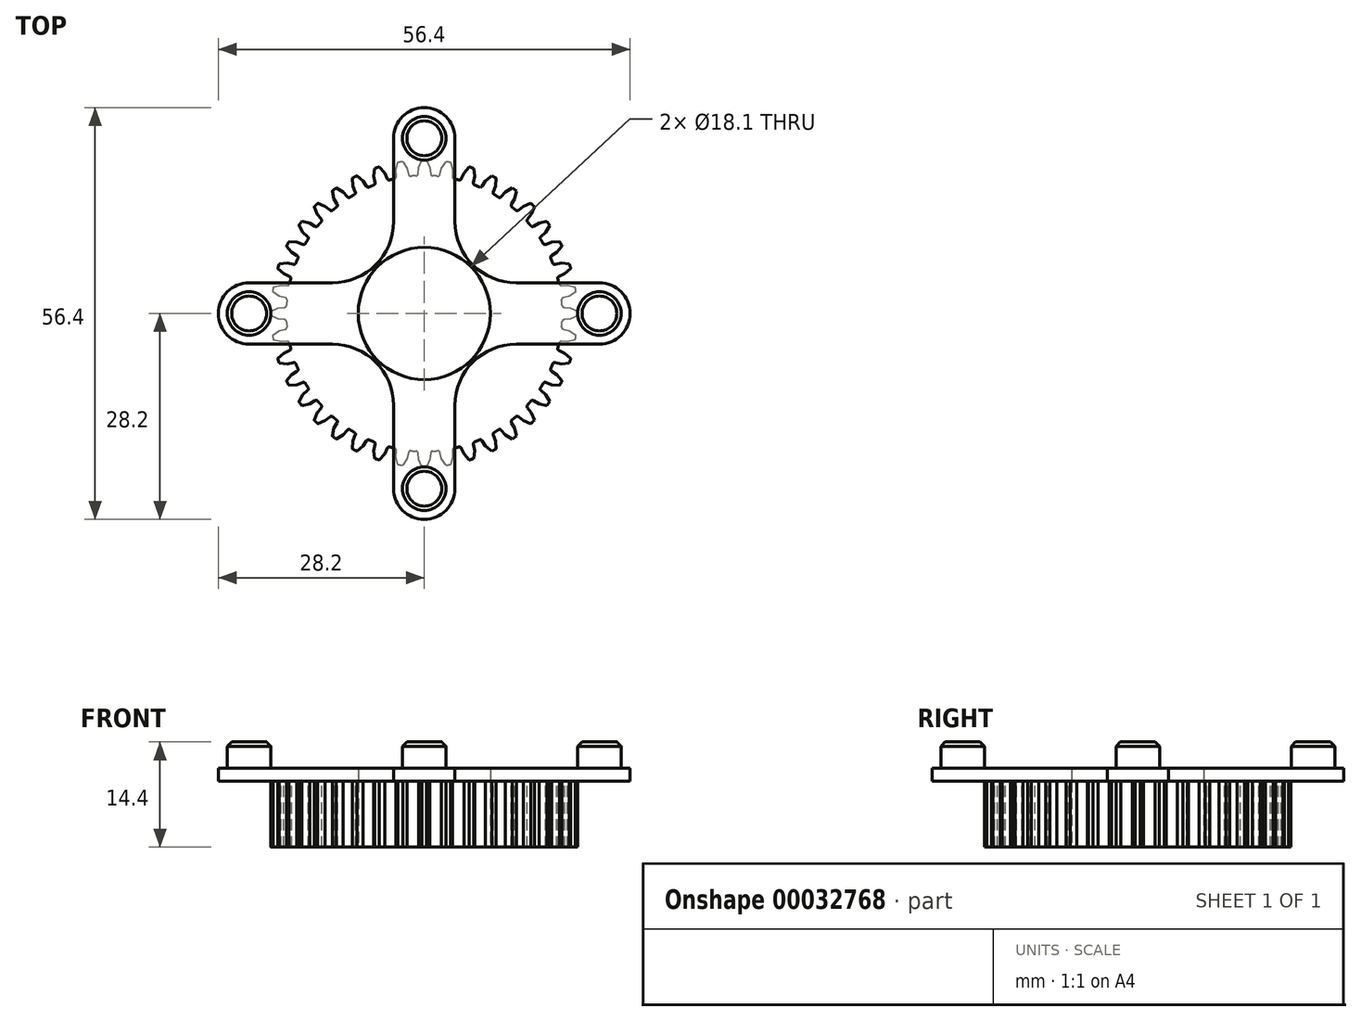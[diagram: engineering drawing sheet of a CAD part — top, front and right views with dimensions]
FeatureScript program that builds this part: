
annotation { "Feature Type Name" : "Feature", "Feature Type Description" : "" }
export const myFeature = defineFeature(function(context is Context, id is Id, definition is map)
    precondition{}
    {
        {
            var Q0;
            Q0=qCreatedBy(makeId("Top.planeOp"),FACE);
            var sketch = newSketch(context, id + "F0", { "sketchPlane" : qUnion([Q0])});
            skCircle(sketch, "E0", {"center": v(0, 0) * mm, "radius": 1 * mm});
            skCircle(sketch, "E1", {"center": v(0, 0) * mm, "radius": 52.75 * mm});
            skCircle(sketch, "E2", {"center": v(0, 40) * mm, "radius": 1 * mm});
            skCircle(sketch, "E3", {"center": v(40, 0) * mm, "radius": 1 * mm});
            skCircle(sketch, "E4", {"center": v(0, -40) * mm, "radius": 1 * mm});
            skCircle(sketch, "E5", {"center": v(-40, 0) * mm, "radius": 1 * mm});
            skCircle(sketch, "E6", {"center": v(0, 40) * mm, "radius": 4.97 * mm});
            skCircle(sketch, "E7", {"center": v(-40, 0) * mm, "radius": 4.97 * mm});
            skCircle(sketch, "E8", {"center": v(40, 0) * mm, "radius": 4.97 * mm});
            skCircle(sketch, "E9", {"center": v(0, -40) * mm, "radius": 4.97 * mm});
            skCircle(sketch, "E10", {"center": v(0, 0) * mm, "radius": 40 * mm, "construction": true});
            skArc(sketch, "E11.0.startCap", {"start": v(-7, 40) * mm, "mid": v(0, 47) * mm, "end": v(7, 40) * mm});
            skArc(sketch, "E11.0.endCap", {"start": v(7, -40) * mm, "mid": v(0, -47) * mm, "end": v(-7, -40) * mm});
            skLineSegment(sketch, "E11.0.left", {"start": v(7, 40) * mm, "end": v(7, 21) * mm});
            skLineSegment(sketch, "E11.0.right", {"start": v(-7, 40) * mm, "end": v(-7, 21) * mm});
            skArc(sketch, "E12.0.startCap", {"start": v(40, 7) * mm, "mid": v(47, 0) * mm, "end": v(40, -7) * mm});
            skArc(sketch, "E12.0.endCap", {"start": v(-40, -7) * mm, "mid": v(-47, 0) * mm, "end": v(-40, 7) * mm});
            skLineSegment(sketch, "E12.0.left", {"start": v(40, -7) * mm, "end": v(21, -7) * mm});
            skLineSegment(sketch, "E12.0.right", {"start": v(40, 7) * mm, "end": v(21, 7) * mm});
            skLineSegment(sketch, "E13.trimOffspring", {"start": v(-21, 7) * mm, "end": v(-40, 7) * mm});
            skLineSegment(sketch, "E14.trimOffspring", {"start": v(-7, -21) * mm, "end": v(-7, -40) * mm});
            skLineSegment(sketch, "E15.trimOffspring", {"start": v(7, -21) * mm, "end": v(7, -40) * mm});
            skLineSegment(sketch, "E16.trimOffspring", {"start": v(-21, -7) * mm, "end": v(-40, -7) * mm});
            skPoint(sketch, "E17.visualSharp", {"position": v(-7, 7) * mm});
            skArc(sketch, "E17.filletArc", {"start": v(-21, 7) * mm, "mid": v(-11.1, 11.1) * mm, "end": v(-7, 21) * mm});
            skPoint(sketch, "E18.visualSharp", {"position": v(-7, -7) * mm});
            skArc(sketch, "E18.filletArc", {"start": v(-7, -21) * mm, "mid": v(-11.1, -11.1) * mm, "end": v(-21, -7) * mm});
            skPoint(sketch, "E19.visualSharp", {"position": v(7, -7) * mm});
            skArc(sketch, "E19.filletArc", {"start": v(21, -7) * mm, "mid": v(11.1, -11.1) * mm, "end": v(7, -21) * mm});
            skPoint(sketch, "E20.visualSharp", {"position": v(7, 7) * mm});
            skArc(sketch, "E20.filletArc", {"start": v(7, 21) * mm, "mid": v(11.1, 11.1) * mm, "end": v(21, 7) * mm});
            skCircle(sketch, "E21", {"center": v(0, 0) * mm, "radius": 5 * mm});
            skCircle(sketch, "E22", {"center": v(0, 0) * mm, "radius": 14 * mm});
            skCircle(sketch, "E23", {"center": v(0, 0) * mm, "radius": 47 * mm, "construction": true});
            skSolve(sketch);
        }
        {
            var Q0;
            Q0=makeQuery(id+"F0.imprint","IMPRINT",FACE,{"disambiguationData":[TD([[makeQuery(id+"F0.imprint","IMPRINT",EDGE,{"derivedFrom":sQuery(id+"F0.wireOp",EDGE,"E6")}),-1.0]])]});
            var Q1;
            Q1=makeQuery(id+"F0.imprint","IMPRINT",FACE,{"disambiguationData":[TD([[makeQuery(id+"F0.imprint","IMPRINT",EDGE,{"derivedFrom":sQuery(id+"F0.wireOp",EDGE,"E5")}),1.0]])]});
            var Q2;
            Q2=makeQuery(id+"F0.imprint","IMPRINT",FACE,{"disambiguationData":[TD([[makeQuery(id+"F0.imprint","IMPRINT",EDGE,{"derivedFrom":sQuery(id+"F0.wireOp",EDGE,"E21")}),-1.0]])]});
            var Q3;
            Q3=makeQuery(id+"F0.imprint","IMPRINT",FACE,{"disambiguationData":[TD([[makeQuery(id+"F0.imprint","IMPRINT",EDGE,{"derivedFrom":sQuery(id+"F0.wireOp",EDGE,"E3")}),1.0]])]});
            var Q4;
            Q4=makeQuery(id+"F0.imprint","IMPRINT",FACE,{"disambiguationData":[TD([[makeQuery(id+"F0.imprint","IMPRINT",EDGE,{"derivedFrom":sQuery(id+"F0.wireOp",EDGE,"E2")}),1.0]])]});
            var Q5;
            Q5=makeQuery(id+"F0.imprint","IMPRINT",FACE,{"disambiguationData":[TD([[makeQuery(id+"F0.imprint","IMPRINT",EDGE,{"derivedFrom":sQuery(id+"F0.wireOp",EDGE,"E4")}),1.0]])]});
            var Q6;
            Q6=makeQuery(id+"F0.imprint","IMPRINT",FACE,{"disambiguationData":[TD([[makeQuery(id+"F0.imprint","IMPRINT",EDGE,{"derivedFrom":sQuery(id+"F0.wireOp",EDGE,"E5")}),-1.0]])]});
            var Q7;
            Q7=makeQuery(id+"F0.imprint","IMPRINT",FACE,{"disambiguationData":[TD([[makeQuery(id+"F0.imprint","IMPRINT",EDGE,{"derivedFrom":sQuery(id+"F0.wireOp",EDGE,"E4")}),-1.0]])]});
            var Q8;
            Q8=makeQuery(id+"F0.imprint","IMPRINT",FACE,{"disambiguationData":[TD([[makeQuery(id+"F0.imprint","IMPRINT",EDGE,{"derivedFrom":sQuery(id+"F0.wireOp",EDGE,"E3")}),-1.0]])]});
            var Q9;
            Q9=makeQuery(id+"F0.imprint","IMPRINT",FACE,{"disambiguationData":[TD([[makeQuery(id+"F0.imprint","IMPRINT",EDGE,{"derivedFrom":sQuery(id+"F0.wireOp",EDGE,"E2")}),-1.0]])]});
            extrude(context, id + "F1", {"entities" : qUnion([Q0, Q1, Q2, Q3, Q4, Q5, Q6, Q7, Q8, Q9]), "depth" : 3 * mm});
        }
        {
            var Q0;
            Q0=makeQuery(id+"F0.imprint","IMPRINT",FACE,{"disambiguationData":[TD([[makeQuery(id+"F0.imprint","IMPRINT",EDGE,{"derivedFrom":sQuery(id+"F0.wireOp",EDGE,"E5")}),1.0]])]});
            var Q1;
            Q1=makeQuery(id+"F0.imprint","IMPRINT",FACE,{"disambiguationData":[TD([[makeQuery(id+"F0.imprint","IMPRINT",EDGE,{"derivedFrom":sQuery(id+"F0.wireOp",EDGE,"E5")}),-1.0]])]});
            var Q2;
            Q2=makeQuery(id+"F0.imprint","IMPRINT",FACE,{"disambiguationData":[TD([[makeQuery(id+"F0.imprint","IMPRINT",EDGE,{"derivedFrom":sQuery(id+"F0.wireOp",EDGE,"E4")}),1.0]])]});
            var Q3;
            Q3=makeQuery(id+"F0.imprint","IMPRINT",FACE,{"disambiguationData":[TD([[makeQuery(id+"F0.imprint","IMPRINT",EDGE,{"derivedFrom":sQuery(id+"F0.wireOp",EDGE,"E4")}),-1.0]])]});
            var Q4;
            Q4=makeQuery(id+"F0.imprint","IMPRINT",FACE,{"disambiguationData":[TD([[makeQuery(id+"F0.imprint","IMPRINT",EDGE,{"derivedFrom":sQuery(id+"F0.wireOp",EDGE,"E3")}),-1.0]])]});
            var Q5;
            Q5=makeQuery(id+"F0.imprint","IMPRINT",FACE,{"disambiguationData":[TD([[makeQuery(id+"F0.imprint","IMPRINT",EDGE,{"derivedFrom":sQuery(id+"F0.wireOp",EDGE,"E3")}),1.0]])]});
            var Q6;
            Q6=makeQuery(id+"F0.imprint","IMPRINT",FACE,{"disambiguationData":[TD([[makeQuery(id+"F0.imprint","IMPRINT",EDGE,{"derivedFrom":sQuery(id+"F0.wireOp",EDGE,"E2")}),1.0]])]});
            var Q7;
            Q7=makeQuery(id+"F0.imprint","IMPRINT",FACE,{"disambiguationData":[TD([[makeQuery(id+"F0.imprint","IMPRINT",EDGE,{"derivedFrom":sQuery(id+"F0.wireOp",EDGE,"E2")}),-1.0]])]});
            extrude(context, id + "F2", {"entities" : qUnion([Q0, Q1, Q2, Q3, Q4, Q5, Q6, Q7]), "operationType" : NewBodyOperationType.ADD, "depth" : 9 * mm});
        }
        {
            var Q0;
            Q0=makeQuery(id+"F2.opExtrude","CAP_EDGE",EDGE,{"disambiguationData":[OSD([sQuery(id+"F0.wireOp",EDGE,"E7")])],"isStart":false});
            var Q1;
            Q1=makeQuery(id+"F2.opExtrude","CAP_EDGE",EDGE,{"disambiguationData":[OSD([sQuery(id+"F0.wireOp",EDGE,"E6")])],"isStart":false});
            var Q2;
            Q2=makeQuery(id+"F2.opExtrude","CAP_EDGE",EDGE,{"disambiguationData":[OSD([sQuery(id+"F0.wireOp",EDGE,"E8")])],"isStart":false});
            var Q3;
            Q3=makeQuery(id+"F2.opExtrude","CAP_EDGE",EDGE,{"disambiguationData":[OSD([sQuery(id+"F0.wireOp",EDGE,"E9")])],"isStart":false});
            var Q4;
            Q4=makeQuery(id+"FGKay2Df9lcGa7H_1.opExtrude","CAP_EDGE",EDGE,{"disambiguationData":[OSD([sQuery(id+"F0.wireOp",EDGE,"E21")])],"isStart":false});
            var Q5;
            Q5=makeQuery(id+"FGKay2Df9lcGa7H_1.opExtrude","CAP_EDGE",EDGE,{"disambiguationData":[OSD([sQuery(id+"F0.wireOp",EDGE,"E22")])],"isStart":false});
            chamfer(context, id + "F3", {"entities" : qUnion([Q0, Q1, Q2, Q3, Q4, Q5]), "width" : 1 * mm, "tangentPropagation" : true});
        }
        {
            var Q0;
            Q0=makeQuery(id+"F1.opExtrude","CAP_FACE",FACE,{"disambiguationData":[OSD([sQuery(id+"F0.wireOp",EDGE,"E11.0.startCap"),sQuery(id+"F0.wireOp",EDGE,"E11.0.endCap"),sQuery(id+"F0.wireOp",EDGE,"E11.0.left"),sQuery(id+"F0.wireOp",EDGE,"E11.0.right"),sQuery(id+"F0.wireOp",EDGE,"E12.0.startCap"),sQuery(id+"F0.wireOp",EDGE,"E12.0.endCap"),sQuery(id+"F0.wireOp",EDGE,"E12.0.left"),sQuery(id+"F0.wireOp",EDGE,"E12.0.right"),sQuery(id+"F0.wireOp",EDGE,"E13.trimOffspring"),sQuery(id+"F0.wireOp",EDGE,"E14.trimOffspring"),sQuery(id+"F0.wireOp",EDGE,"E15.trimOffspring"),sQuery(id+"F0.wireOp",EDGE,"E16.trimOffspring"),sQuery(id+"F0.wireOp",EDGE,"E17.filletArc"),sQuery(id+"F0.wireOp",EDGE,"E18.filletArc"),sQuery(id+"F0.wireOp",EDGE,"E19.filletArc"),sQuery(id+"F0.wireOp",EDGE,"E20.filletArc"),sQuery(id+"F0.wireOp",EDGE,"E21")])],"isStart":true});
            var sketch = newSketch(context, id + "F4", { "sketchPlane" : qUnion([Q0])});
            skArc(sketch, "E24", {"start": v(21, -0.33) * mm, "mid": v(21, -0.17) * mm, "end": v(21, 0) * mm});
            skArc(sketch, "E25", {"start": v(-12.5, 0) * mm, "mid": v(0, -12.5) * mm, "end": v(12.5, 0) * mm});
            skArc(sketch, "E26", {"start": v(0, -5) * mm, "mid": v(5, 0) * mm, "end": v(0, 5) * mm});
            skArc(sketch, "E27", {"start": v(-21, 0) * mm, "mid": v(-21, -0.17) * mm, "end": v(-21, -0.33) * mm});
            skArc(sketch, "E28", {"start": v(18.87, 1.14) * mm, "mid": v(18.84, 1.48) * mm, "end": v(18.81, 1.83) * mm});
            skArc(sketch, "E29", {"start": v(19.04, 2.15) * mm, "mid": v(18.86, 2.03) * mm, "end": v(18.81, 1.83) * mm});
            skLineSegment(sketch, "E30", {"start": v(19.04, 2.15) * mm, "end": v(19.86, 2.36) * mm});
            skArc(sketch, "E31", {"start": v(19.14, -0.86) * mm, "mid": v(18.95, -0.95) * mm, "end": v(18.87, -1.14) * mm});
            skLineSegment(sketch, "E32", {"start": v(19.86, 2.36) * mm, "end": v(20.8, 2.96) * mm});
            skArc(sketch, "E33", {"start": v(18.46, 4.07) * mm, "mid": v(18.38, 4.41) * mm, "end": v(18.3, 4.75) * mm});
            skLineSegment(sketch, "E34", {"start": v(19.14, -0.86) * mm, "end": v(19.98, -0.78) * mm});
            skArc(sketch, "E35", {"start": v(18.46, 5.1) * mm, "mid": v(18.31, 4.96) * mm, "end": v(18.3, 4.75) * mm});
            skLineSegment(sketch, "E36", {"start": v(19.98, -0.78) * mm, "end": v(21, -0.33) * mm});
            skLineSegment(sketch, "E37", {"start": v(18.46, 5.1) * mm, "end": v(19.25, 5.44) * mm});
            skArc(sketch, "E38", {"start": v(18.77, -3.84) * mm, "mid": v(18.57, -3.9) * mm, "end": v(18.46, -4.07) * mm});
            skLineSegment(sketch, "E39", {"start": v(19.25, 5.44) * mm, "end": v(20.07, 6.17) * mm});
            skArc(sketch, "E40", {"start": v(17.6, 6.91) * mm, "mid": v(17.46, 7.23) * mm, "end": v(17.33, 7.55) * mm});
            skLineSegment(sketch, "E41", {"start": v(18.77, -3.84) * mm, "end": v(19.62, -3.9) * mm});
            skArc(sketch, "E42", {"start": v(17.44, 7.93) * mm, "mid": v(17.31, 7.76) * mm, "end": v(17.33, 7.55) * mm});
            skLineSegment(sketch, "E43", {"start": v(19.62, -3.9) * mm, "end": v(20.69, -3.61) * mm});
            skLineSegment(sketch, "E44", {"start": v(17.44, 7.93) * mm, "end": v(18.16, 8.38) * mm});
            skArc(sketch, "E45", {"start": v(17.94, -6.73) * mm, "mid": v(17.73, -6.76) * mm, "end": v(17.6, -6.91) * mm});
            skLineSegment(sketch, "E46", {"start": v(18.16, 8.38) * mm, "end": v(18.86, 9.24) * mm});
            skArc(sketch, "E47", {"start": v(16.3, 9.58) * mm, "mid": v(16.11, 9.88) * mm, "end": v(15.93, 10.17) * mm});
            skLineSegment(sketch, "E48", {"start": v(17.94, -6.73) * mm, "end": v(18.77, -6.91) * mm});
            skArc(sketch, "E49", {"start": v(15.98, 10.56) * mm, "mid": v(15.89, 10.37) * mm, "end": v(15.93, 10.17) * mm});
            skLineSegment(sketch, "E50", {"start": v(18.77, -6.91) * mm, "end": v(19.87, -6.8) * mm});
            skLineSegment(sketch, "E51", {"start": v(15.98, 10.56) * mm, "end": v(16.62, 11.12) * mm});
            skArc(sketch, "E52", {"start": v(16.66, -9.45) * mm, "mid": v(16.45, -9.45) * mm, "end": v(16.3, -9.58) * mm});
            skLineSegment(sketch, "E53", {"start": v(16.62, 11.12) * mm, "end": v(17.18, 12.07) * mm});
            skArc(sketch, "E54", {"start": v(14.6, 12) * mm, "mid": v(14.37, 12.27) * mm, "end": v(14.14, 12.54) * mm});
            skLineSegment(sketch, "E55", {"start": v(16.66, -9.45) * mm, "end": v(17.45, -9.76) * mm});
            skArc(sketch, "E56", {"start": v(14.14, 12.93) * mm, "mid": v(14.07, 12.73) * mm, "end": v(14.14, 12.54) * mm});
            skLineSegment(sketch, "E57", {"start": v(17.45, -9.76) * mm, "end": v(18.56, -9.83) * mm});
            skLineSegment(sketch, "E58", {"start": v(14.14, 12.93) * mm, "end": v(14.68, 13.58) * mm});
            skArc(sketch, "E59", {"start": v(14.98, -11.94) * mm, "mid": v(14.77, -11.9) * mm, "end": v(14.6, -12) * mm});
            skLineSegment(sketch, "E60", {"start": v(14.68, 13.58) * mm, "end": v(15.08, 14.61) * mm});
            skArc(sketch, "E61", {"start": v(12.54, 14.14) * mm, "mid": v(12.27, 14.37) * mm, "end": v(12, 14.6) * mm});
            skLineSegment(sketch, "E62", {"start": v(14.98, -11.94) * mm, "end": v(15.71, -12.37) * mm});
            skArc(sketch, "E63", {"start": v(11.94, 14.98) * mm, "mid": v(11.9, 14.77) * mm, "end": v(12, 14.6) * mm});
            skLineSegment(sketch, "E64", {"start": v(15.71, -12.37) * mm, "end": v(16.8, -12.61) * mm});
            skArc(sketch, "E65", {"start": v(12.93, -14.14) * mm, "mid": v(12.73, -14.07) * mm, "end": v(12.54, -14.14) * mm});
            skLineSegment(sketch, "E66", {"start": v(11.94, 14.98) * mm, "end": v(12.37, 15.71) * mm});
            skLineSegment(sketch, "E67", {"start": v(12.93, -14.14) * mm, "end": v(13.58, -14.68) * mm});
            skLineSegment(sketch, "E68", {"start": v(12.37, 15.71) * mm, "end": v(12.61, 16.8) * mm});
            skArc(sketch, "E69", {"start": v(10.17, 15.93) * mm, "mid": v(9.88, 16.11) * mm, "end": v(9.58, 16.3) * mm});
            skLineSegment(sketch, "E70", {"start": v(13.58, -14.68) * mm, "end": v(14.61, -15.08) * mm});
            skArc(sketch, "E71", {"start": v(9.45, 16.66) * mm, "mid": v(9.45, 16.45) * mm, "end": v(9.58, 16.3) * mm});
            skArc(sketch, "E72", {"start": v(10.56, -15.98) * mm, "mid": v(10.37, -15.89) * mm, "end": v(10.17, -15.93) * mm});
            skLineSegment(sketch, "E73", {"start": v(9.45, 16.66) * mm, "end": v(9.76, 17.45) * mm});
            skLineSegment(sketch, "E74", {"start": v(10.56, -15.98) * mm, "end": v(11.12, -16.62) * mm});
            skLineSegment(sketch, "E75", {"start": v(9.76, 17.45) * mm, "end": v(9.83, 18.56) * mm});
            skArc(sketch, "E76", {"start": v(7.55, 17.33) * mm, "mid": v(7.23, 17.46) * mm, "end": v(6.91, 17.6) * mm});
            skLineSegment(sketch, "E77", {"start": v(11.12, -16.62) * mm, "end": v(12.07, -17.18) * mm});
            skArc(sketch, "E78", {"start": v(6.73, 17.94) * mm, "mid": v(6.76, 17.73) * mm, "end": v(6.91, 17.6) * mm});
            skArc(sketch, "E79", {"start": v(7.93, -17.44) * mm, "mid": v(7.76, -17.31) * mm, "end": v(7.55, -17.33) * mm});
            skLineSegment(sketch, "E80", {"start": v(6.73, 17.94) * mm, "end": v(6.91, 18.77) * mm});
            skLineSegment(sketch, "E81", {"start": v(7.93, -17.44) * mm, "end": v(8.38, -18.16) * mm});
            skLineSegment(sketch, "E82", {"start": v(6.91, 18.77) * mm, "end": v(6.8, 19.87) * mm});
            skArc(sketch, "E83", {"start": v(4.75, 18.3) * mm, "mid": v(4.41, 18.38) * mm, "end": v(4.07, 18.46) * mm});
            skLineSegment(sketch, "E84", {"start": v(8.38, -18.16) * mm, "end": v(9.24, -18.86) * mm});
            skArc(sketch, "E85", {"start": v(3.84, 18.77) * mm, "mid": v(3.9, 18.57) * mm, "end": v(4.07, 18.46) * mm});
            skArc(sketch, "E86", {"start": v(5.1, -18.46) * mm, "mid": v(4.96, -18.31) * mm, "end": v(4.75, -18.3) * mm});
            skLineSegment(sketch, "E87", {"start": v(3.84, 18.77) * mm, "end": v(3.9, 19.62) * mm});
            skLineSegment(sketch, "E88", {"start": v(5.1, -18.46) * mm, "end": v(5.44, -19.25) * mm});
            skLineSegment(sketch, "E89", {"start": v(3.9, 19.62) * mm, "end": v(3.61, 20.69) * mm});
            skArc(sketch, "E90", {"start": v(1.83, 18.81) * mm, "mid": v(1.48, 18.84) * mm, "end": v(1.14, 18.87) * mm});
            skLineSegment(sketch, "E91", {"start": v(5.44, -19.25) * mm, "end": v(6.17, -20.07) * mm});
            skArc(sketch, "E92", {"start": v(0.86, 19.14) * mm, "mid": v(0.95, 18.95) * mm, "end": v(1.14, 18.87) * mm});
            skArc(sketch, "E93", {"start": v(2.15, -19.04) * mm, "mid": v(2.03, -18.86) * mm, "end": v(1.83, -18.81) * mm});
            skLineSegment(sketch, "E94", {"start": v(0.86, 19.14) * mm, "end": v(0.78, 19.98) * mm});
            skArc(sketch, "E95", {"start": v(-1.14, 18.87) * mm, "mid": v(-1.48, 18.84) * mm, "end": v(-1.83, 18.81) * mm});
            skLineSegment(sketch, "E96", {"start": v(2.15, -19.04) * mm, "end": v(2.36, -19.86) * mm});
            skLineSegment(sketch, "E97", {"start": v(0.78, 19.98) * mm, "end": v(0.33, 21) * mm});
            skArc(sketch, "E98", {"start": v(-2.15, 19.04) * mm, "mid": v(-2.03, 18.86) * mm, "end": v(-1.83, 18.81) * mm});
            skLineSegment(sketch, "E99", {"start": v(2.36, -19.86) * mm, "end": v(2.96, -20.8) * mm});
            skArc(sketch, "E100", {"start": v(-0.86, -19.14) * mm, "mid": v(-0.95, -18.95) * mm, "end": v(-1.14, -18.87) * mm});
            skLineSegment(sketch, "E101", {"start": v(-2.15, 19.04) * mm, "end": v(-2.36, 19.86) * mm});
            skLineSegment(sketch, "E102", {"start": v(-0.86, -19.14) * mm, "end": v(-0.78, -19.98) * mm});
            skLineSegment(sketch, "E103", {"start": v(-2.36, 19.86) * mm, "end": v(-2.96, 20.8) * mm});
            skArc(sketch, "E104", {"start": v(-4.07, 18.46) * mm, "mid": v(-4.41, 18.38) * mm, "end": v(-4.75, 18.3) * mm});
            skLineSegment(sketch, "E105", {"start": v(-0.78, -19.98) * mm, "end": v(-0.33, -21) * mm});
            skArc(sketch, "E106", {"start": v(-5.1, 18.46) * mm, "mid": v(-4.96, 18.31) * mm, "end": v(-4.75, 18.3) * mm});
            skArc(sketch, "E107", {"start": v(-3.84, -18.77) * mm, "mid": v(-3.9, -18.57) * mm, "end": v(-4.07, -18.46) * mm});
            skLineSegment(sketch, "E108", {"start": v(-5.1, 18.46) * mm, "end": v(-5.44, 19.25) * mm});
            skLineSegment(sketch, "E109", {"start": v(-3.84, -18.77) * mm, "end": v(-3.9, -19.62) * mm});
            skLineSegment(sketch, "E110", {"start": v(-5.44, 19.25) * mm, "end": v(-6.17, 20.07) * mm});
            skArc(sketch, "E111", {"start": v(-6.91, 17.6) * mm, "mid": v(-7.23, 17.46) * mm, "end": v(-7.55, 17.33) * mm});
            skLineSegment(sketch, "E112", {"start": v(-3.9, -19.62) * mm, "end": v(-3.61, -20.69) * mm});
            skArc(sketch, "E113", {"start": v(-7.93, 17.44) * mm, "mid": v(-7.76, 17.31) * mm, "end": v(-7.55, 17.33) * mm});
            skArc(sketch, "E114", {"start": v(-6.73, -17.94) * mm, "mid": v(-6.76, -17.73) * mm, "end": v(-6.91, -17.6) * mm});
            skLineSegment(sketch, "E115", {"start": v(-7.93, 17.44) * mm, "end": v(-8.38, 18.16) * mm});
            skLineSegment(sketch, "E116", {"start": v(-6.73, -17.94) * mm, "end": v(-6.91, -18.77) * mm});
            skLineSegment(sketch, "E117", {"start": v(-8.38, 18.16) * mm, "end": v(-9.24, 18.86) * mm});
            skArc(sketch, "E118", {"start": v(-9.58, 16.3) * mm, "mid": v(-9.88, 16.11) * mm, "end": v(-10.17, 15.93) * mm});
            skLineSegment(sketch, "E119", {"start": v(-6.91, -18.77) * mm, "end": v(-6.8, -19.87) * mm});
            skArc(sketch, "E120", {"start": v(-10.56, 15.98) * mm, "mid": v(-10.37, 15.89) * mm, "end": v(-10.17, 15.93) * mm});
            skArc(sketch, "E121", {"start": v(-9.45, -16.66) * mm, "mid": v(-9.45, -16.45) * mm, "end": v(-9.58, -16.3) * mm});
            skLineSegment(sketch, "E122", {"start": v(-10.56, 15.98) * mm, "end": v(-11.12, 16.62) * mm});
            skLineSegment(sketch, "E123", {"start": v(-9.45, -16.66) * mm, "end": v(-9.76, -17.45) * mm});
            skLineSegment(sketch, "E124", {"start": v(-11.12, 16.62) * mm, "end": v(-12.07, 17.18) * mm});
            skArc(sketch, "E125", {"start": v(-12, 14.6) * mm, "mid": v(-12.27, 14.37) * mm, "end": v(-12.54, 14.14) * mm});
            skLineSegment(sketch, "E126", {"start": v(-9.76, -17.45) * mm, "end": v(-9.83, -18.56) * mm});
            skArc(sketch, "E127", {"start": v(-12.93, 14.14) * mm, "mid": v(-12.73, 14.07) * mm, "end": v(-12.54, 14.14) * mm});
            skArc(sketch, "E128", {"start": v(-11.94, -14.98) * mm, "mid": v(-11.9, -14.77) * mm, "end": v(-12, -14.6) * mm});
            skLineSegment(sketch, "E129", {"start": v(-12.93, 14.14) * mm, "end": v(-13.58, 14.68) * mm});
            skLineSegment(sketch, "E130", {"start": v(-11.94, -14.98) * mm, "end": v(-12.37, -15.71) * mm});
            skLineSegment(sketch, "E131", {"start": v(-13.58, 14.68) * mm, "end": v(-14.61, 15.08) * mm});
            skArc(sketch, "E132", {"start": v(-14.14, 12.54) * mm, "mid": v(-14.37, 12.27) * mm, "end": v(-14.6, 12) * mm});
            skLineSegment(sketch, "E133", {"start": v(-12.37, -15.71) * mm, "end": v(-12.61, -16.8) * mm});
            skArc(sketch, "E134", {"start": v(-14.98, 11.94) * mm, "mid": v(-14.77, 11.9) * mm, "end": v(-14.6, 12) * mm});
            skArc(sketch, "E135", {"start": v(-14.14, -12.93) * mm, "mid": v(-14.07, -12.73) * mm, "end": v(-14.14, -12.54) * mm});
            skLineSegment(sketch, "E136", {"start": v(-14.98, 11.94) * mm, "end": v(-15.71, 12.37) * mm});
            skLineSegment(sketch, "E137", {"start": v(-14.14, -12.93) * mm, "end": v(-14.68, -13.58) * mm});
            skLineSegment(sketch, "E138", {"start": v(-15.71, 12.37) * mm, "end": v(-16.8, 12.61) * mm});
            skArc(sketch, "E139", {"start": v(-15.93, 10.17) * mm, "mid": v(-16.11, 9.88) * mm, "end": v(-16.3, 9.58) * mm});
            skLineSegment(sketch, "E140", {"start": v(-14.68, -13.58) * mm, "end": v(-15.08, -14.61) * mm});
            skArc(sketch, "E141", {"start": v(-16.66, 9.45) * mm, "mid": v(-16.45, 9.45) * mm, "end": v(-16.3, 9.58) * mm});
            skArc(sketch, "E142", {"start": v(-15.98, -10.56) * mm, "mid": v(-15.89, -10.37) * mm, "end": v(-15.93, -10.17) * mm});
            skLineSegment(sketch, "E143", {"start": v(-16.66, 9.45) * mm, "end": v(-17.45, 9.76) * mm});
            skLineSegment(sketch, "E144", {"start": v(-15.98, -10.56) * mm, "end": v(-16.62, -11.12) * mm});
            skLineSegment(sketch, "E145", {"start": v(-17.45, 9.76) * mm, "end": v(-18.56, 9.83) * mm});
            skArc(sketch, "E146", {"start": v(-17.33, 7.55) * mm, "mid": v(-17.46, 7.23) * mm, "end": v(-17.6, 6.91) * mm});
            skLineSegment(sketch, "E147", {"start": v(-16.62, -11.12) * mm, "end": v(-17.18, -12.07) * mm});
            skArc(sketch, "E148", {"start": v(-17.94, 6.73) * mm, "mid": v(-17.73, 6.76) * mm, "end": v(-17.6, 6.91) * mm});
            skArc(sketch, "E149", {"start": v(-17.44, -7.93) * mm, "mid": v(-17.31, -7.76) * mm, "end": v(-17.33, -7.55) * mm});
            skLineSegment(sketch, "E150", {"start": v(-17.94, 6.73) * mm, "end": v(-18.77, 6.91) * mm});
            skLineSegment(sketch, "E151", {"start": v(-17.44, -7.93) * mm, "end": v(-18.16, -8.38) * mm});
            skLineSegment(sketch, "E152", {"start": v(-18.77, 6.91) * mm, "end": v(-19.87, 6.8) * mm});
            skArc(sketch, "E153", {"start": v(-18.3, 4.75) * mm, "mid": v(-18.38, 4.41) * mm, "end": v(-18.46, 4.07) * mm});
            skLineSegment(sketch, "E154", {"start": v(-18.16, -8.38) * mm, "end": v(-18.86, -9.24) * mm});
            skArc(sketch, "E155", {"start": v(-18.77, 3.84) * mm, "mid": v(-18.57, 3.9) * mm, "end": v(-18.46, 4.07) * mm});
            skArc(sketch, "E156", {"start": v(-18.46, -5.1) * mm, "mid": v(-18.31, -4.96) * mm, "end": v(-18.3, -4.75) * mm});
            skLineSegment(sketch, "E157", {"start": v(-18.77, 3.84) * mm, "end": v(-19.62, 3.9) * mm});
            skLineSegment(sketch, "E158", {"start": v(-18.46, -5.1) * mm, "end": v(-19.25, -5.44) * mm});
            skLineSegment(sketch, "E159", {"start": v(-19.62, 3.9) * mm, "end": v(-20.69, 3.61) * mm});
            skArc(sketch, "E160", {"start": v(-18.81, 1.83) * mm, "mid": v(-18.84, 1.48) * mm, "end": v(-18.87, 1.14) * mm});
            skLineSegment(sketch, "E161", {"start": v(-19.25, -5.44) * mm, "end": v(-20.07, -6.17) * mm});
            skArc(sketch, "E162", {"start": v(-19.14, 0.86) * mm, "mid": v(-18.95, 0.95) * mm, "end": v(-18.87, 1.14) * mm});
            skLineSegment(sketch, "E163", {"start": v(-19.14, 0.86) * mm, "end": v(-19.98, 0.78) * mm});
            skArc(sketch, "E164", {"start": v(-19.04, -2.15) * mm, "mid": v(-18.86, -2.03) * mm, "end": v(-18.81, -1.83) * mm});
            skLineSegment(sketch, "E165", {"start": v(-19.04, -2.15) * mm, "end": v(-19.86, -2.36) * mm});
            skLineSegment(sketch, "E166", {"start": v(-19.98, 0.78) * mm, "end": v(-21, 0.33) * mm});
            skLineSegment(sketch, "E167", {"start": v(-19.86, -2.36) * mm, "end": v(-20.8, -2.96) * mm});
            skLineSegment(sketch, "E168", {"start": v(-21, -0.33) * mm, "end": v(-19.98, -0.78) * mm});
            skLineSegment(sketch, "E169", {"start": v(-19.98, -0.78) * mm, "end": v(-19.14, -0.86) * mm});
            skArc(sketch, "E170", {"start": v(-18.87, -1.14) * mm, "mid": v(-18.95, -0.95) * mm, "end": v(-19.14, -0.86) * mm});
            skArc(sketch, "E171", {"start": v(-18.87, -1.14) * mm, "mid": v(-18.84, -1.48) * mm, "end": v(-18.81, -1.83) * mm});
            skLineSegment(sketch, "E172", {"start": v(-20.69, -3.61) * mm, "end": v(-19.62, -3.9) * mm});
            skLineSegment(sketch, "E173", {"start": v(-19.62, -3.9) * mm, "end": v(-18.77, -3.84) * mm});
            skArc(sketch, "E174", {"start": v(-18.46, -4.07) * mm, "mid": v(-18.57, -3.9) * mm, "end": v(-18.77, -3.84) * mm});
            skArc(sketch, "E175", {"start": v(-18.46, -4.07) * mm, "mid": v(-18.38, -4.41) * mm, "end": v(-18.3, -4.75) * mm});
            skLineSegment(sketch, "E176", {"start": v(-19.87, -6.8) * mm, "end": v(-18.77, -6.91) * mm});
            skLineSegment(sketch, "E177", {"start": v(-18.77, -6.91) * mm, "end": v(-17.94, -6.73) * mm});
            skArc(sketch, "E178", {"start": v(-17.6, -6.91) * mm, "mid": v(-17.73, -6.76) * mm, "end": v(-17.94, -6.73) * mm});
            skArc(sketch, "E179", {"start": v(-17.6, -6.91) * mm, "mid": v(-17.46, -7.23) * mm, "end": v(-17.33, -7.55) * mm});
            skLineSegment(sketch, "E180", {"start": v(-18.56, -9.83) * mm, "end": v(-17.45, -9.76) * mm});
            skLineSegment(sketch, "E181", {"start": v(-17.45, -9.76) * mm, "end": v(-16.66, -9.45) * mm});
            skArc(sketch, "E182", {"start": v(-16.3, -9.58) * mm, "mid": v(-16.45, -9.45) * mm, "end": v(-16.66, -9.45) * mm});
            skArc(sketch, "E183", {"start": v(-16.3, -9.58) * mm, "mid": v(-16.11, -9.88) * mm, "end": v(-15.93, -10.17) * mm});
            skLineSegment(sketch, "E184", {"start": v(-16.8, -12.61) * mm, "end": v(-15.71, -12.37) * mm});
            skLineSegment(sketch, "E185", {"start": v(-15.71, -12.37) * mm, "end": v(-14.98, -11.94) * mm});
            skArc(sketch, "E186", {"start": v(-14.6, -12) * mm, "mid": v(-14.77, -11.9) * mm, "end": v(-14.98, -11.94) * mm});
            skArc(sketch, "E187", {"start": v(-14.6, -12) * mm, "mid": v(-14.37, -12.27) * mm, "end": v(-14.14, -12.54) * mm});
            skLineSegment(sketch, "E188", {"start": v(-14.61, -15.08) * mm, "end": v(-13.58, -14.68) * mm});
            skLineSegment(sketch, "E189", {"start": v(-13.58, -14.68) * mm, "end": v(-12.93, -14.14) * mm});
            skArc(sketch, "E190", {"start": v(-12.54, -14.14) * mm, "mid": v(-12.73, -14.07) * mm, "end": v(-12.93, -14.14) * mm});
            skArc(sketch, "E191", {"start": v(-12.54, -14.14) * mm, "mid": v(-12.27, -14.37) * mm, "end": v(-12, -14.6) * mm});
            skLineSegment(sketch, "E192", {"start": v(-12.07, -17.18) * mm, "end": v(-11.12, -16.62) * mm});
            skLineSegment(sketch, "E193", {"start": v(-11.12, -16.62) * mm, "end": v(-10.56, -15.98) * mm});
            skArc(sketch, "E194", {"start": v(-10.17, -15.93) * mm, "mid": v(-10.37, -15.89) * mm, "end": v(-10.56, -15.98) * mm});
            skArc(sketch, "E195", {"start": v(-10.17, -15.93) * mm, "mid": v(-9.88, -16.11) * mm, "end": v(-9.58, -16.3) * mm});
            skLineSegment(sketch, "E196", {"start": v(-9.24, -18.86) * mm, "end": v(-8.38, -18.16) * mm});
            skLineSegment(sketch, "E197", {"start": v(-8.38, -18.16) * mm, "end": v(-7.93, -17.44) * mm});
            skArc(sketch, "E198", {"start": v(-7.55, -17.33) * mm, "mid": v(-7.76, -17.31) * mm, "end": v(-7.93, -17.44) * mm});
            skArc(sketch, "E199", {"start": v(-7.55, -17.33) * mm, "mid": v(-7.23, -17.46) * mm, "end": v(-6.91, -17.6) * mm});
            skLineSegment(sketch, "E200", {"start": v(-6.17, -20.07) * mm, "end": v(-5.44, -19.25) * mm});
            skLineSegment(sketch, "E201", {"start": v(-5.44, -19.25) * mm, "end": v(-5.1, -18.46) * mm});
            skArc(sketch, "E202", {"start": v(-4.75, -18.3) * mm, "mid": v(-4.96, -18.31) * mm, "end": v(-5.1, -18.46) * mm});
            skArc(sketch, "E203", {"start": v(-4.75, -18.3) * mm, "mid": v(-4.41, -18.38) * mm, "end": v(-4.07, -18.46) * mm});
            skLineSegment(sketch, "E204", {"start": v(-2.96, -20.8) * mm, "end": v(-2.36, -19.86) * mm});
            skLineSegment(sketch, "E205", {"start": v(-2.36, -19.86) * mm, "end": v(-2.15, -19.04) * mm});
            skArc(sketch, "E206", {"start": v(-1.83, -18.81) * mm, "mid": v(-2.03, -18.86) * mm, "end": v(-2.15, -19.04) * mm});
            skArc(sketch, "E207", {"start": v(-1.83, -18.81) * mm, "mid": v(-1.48, -18.84) * mm, "end": v(-1.14, -18.87) * mm});
            skLineSegment(sketch, "E208", {"start": v(0.33, -21) * mm, "end": v(0.78, -19.98) * mm});
            skLineSegment(sketch, "E209", {"start": v(0.78, -19.98) * mm, "end": v(0.86, -19.14) * mm});
            skArc(sketch, "E210", {"start": v(1.14, -18.87) * mm, "mid": v(0.95, -18.95) * mm, "end": v(0.86, -19.14) * mm});
            skArc(sketch, "E211", {"start": v(1.14, -18.87) * mm, "mid": v(1.48, -18.84) * mm, "end": v(1.83, -18.81) * mm});
            skLineSegment(sketch, "E212", {"start": v(3.61, -20.69) * mm, "end": v(3.9, -19.62) * mm});
            skLineSegment(sketch, "E213", {"start": v(3.9, -19.62) * mm, "end": v(3.84, -18.77) * mm});
            skArc(sketch, "E214", {"start": v(4.07, -18.46) * mm, "mid": v(3.9, -18.57) * mm, "end": v(3.84, -18.77) * mm});
            skArc(sketch, "E215", {"start": v(4.07, -18.46) * mm, "mid": v(4.41, -18.38) * mm, "end": v(4.75, -18.3) * mm});
            skLineSegment(sketch, "E216", {"start": v(6.8, -19.87) * mm, "end": v(6.91, -18.77) * mm});
            skLineSegment(sketch, "E217", {"start": v(6.91, -18.77) * mm, "end": v(6.73, -17.94) * mm});
            skArc(sketch, "E218", {"start": v(6.91, -17.6) * mm, "mid": v(6.76, -17.73) * mm, "end": v(6.73, -17.94) * mm});
            skArc(sketch, "E219", {"start": v(6.91, -17.6) * mm, "mid": v(7.23, -17.46) * mm, "end": v(7.55, -17.33) * mm});
            skLineSegment(sketch, "E220", {"start": v(9.83, -18.56) * mm, "end": v(9.76, -17.45) * mm});
            skLineSegment(sketch, "E221", {"start": v(9.76, -17.45) * mm, "end": v(9.45, -16.66) * mm});
            skArc(sketch, "E222", {"start": v(9.58, -16.3) * mm, "mid": v(9.45, -16.45) * mm, "end": v(9.45, -16.66) * mm});
            skArc(sketch, "E223", {"start": v(9.58, -16.3) * mm, "mid": v(9.88, -16.11) * mm, "end": v(10.17, -15.93) * mm});
            skLineSegment(sketch, "E224", {"start": v(12.61, -16.8) * mm, "end": v(12.37, -15.71) * mm});
            skLineSegment(sketch, "E225", {"start": v(12.37, -15.71) * mm, "end": v(11.94, -14.98) * mm});
            skArc(sketch, "E226", {"start": v(12, -14.6) * mm, "mid": v(11.9, -14.77) * mm, "end": v(11.94, -14.98) * mm});
            skArc(sketch, "E227", {"start": v(12, -14.6) * mm, "mid": v(12.27, -14.37) * mm, "end": v(12.54, -14.14) * mm});
            skLineSegment(sketch, "E228", {"start": v(15.08, -14.61) * mm, "end": v(14.68, -13.58) * mm});
            skLineSegment(sketch, "E229", {"start": v(14.68, -13.58) * mm, "end": v(14.14, -12.93) * mm});
            skArc(sketch, "E230", {"start": v(14.14, -12.54) * mm, "mid": v(14.07, -12.73) * mm, "end": v(14.14, -12.93) * mm});
            skArc(sketch, "E231", {"start": v(14.14, -12.54) * mm, "mid": v(14.37, -12.27) * mm, "end": v(14.6, -12) * mm});
            skLineSegment(sketch, "E232", {"start": v(17.18, -12.07) * mm, "end": v(16.62, -11.12) * mm});
            skLineSegment(sketch, "E233", {"start": v(16.62, -11.12) * mm, "end": v(15.98, -10.56) * mm});
            skArc(sketch, "E234", {"start": v(15.93, -10.17) * mm, "mid": v(15.89, -10.37) * mm, "end": v(15.98, -10.56) * mm});
            skArc(sketch, "E235", {"start": v(15.93, -10.17) * mm, "mid": v(16.11, -9.88) * mm, "end": v(16.3, -9.58) * mm});
            skLineSegment(sketch, "E236", {"start": v(18.86, -9.24) * mm, "end": v(18.16, -8.38) * mm});
            skLineSegment(sketch, "E237", {"start": v(18.16, -8.38) * mm, "end": v(17.44, -7.93) * mm});
            skArc(sketch, "E238", {"start": v(17.33, -7.55) * mm, "mid": v(17.31, -7.76) * mm, "end": v(17.44, -7.93) * mm});
            skArc(sketch, "E239", {"start": v(17.33, -7.55) * mm, "mid": v(17.46, -7.23) * mm, "end": v(17.6, -6.91) * mm});
            skLineSegment(sketch, "E240", {"start": v(20.07, -6.17) * mm, "end": v(19.25, -5.44) * mm});
            skLineSegment(sketch, "E241", {"start": v(19.25, -5.44) * mm, "end": v(18.46, -5.1) * mm});
            skArc(sketch, "E242", {"start": v(18.3, -4.75) * mm, "mid": v(18.31, -4.96) * mm, "end": v(18.46, -5.1) * mm});
            skArc(sketch, "E243", {"start": v(18.3, -4.75) * mm, "mid": v(18.38, -4.41) * mm, "end": v(18.46, -4.07) * mm});
            skLineSegment(sketch, "E244", {"start": v(20.8, -2.96) * mm, "end": v(19.86, -2.36) * mm});
            skLineSegment(sketch, "E245", {"start": v(19.86, -2.36) * mm, "end": v(19.04, -2.15) * mm});
            skArc(sketch, "E246", {"start": v(18.81, -1.83) * mm, "mid": v(18.86, -2.03) * mm, "end": v(19.04, -2.15) * mm});
            skArc(sketch, "E247", {"start": v(18.81, -1.83) * mm, "mid": v(18.84, -1.48) * mm, "end": v(18.87, -1.14) * mm});
            skLineSegment(sketch, "E248", {"start": v(21, 0.33) * mm, "end": v(19.98, 0.78) * mm});
            skLineSegment(sketch, "E249", {"start": v(19.98, 0.78) * mm, "end": v(19.14, 0.86) * mm});
            skArc(sketch, "E250", {"start": v(18.87, 1.14) * mm, "mid": v(18.95, 0.95) * mm, "end": v(19.14, 0.86) * mm});
            skLineSegment(sketch, "E251", {"start": v(20.69, 3.61) * mm, "end": v(19.62, 3.9) * mm});
            skLineSegment(sketch, "E252", {"start": v(19.62, 3.9) * mm, "end": v(18.77, 3.84) * mm});
            skArc(sketch, "E253", {"start": v(18.46, 4.07) * mm, "mid": v(18.57, 3.9) * mm, "end": v(18.77, 3.84) * mm});
            skLineSegment(sketch, "E254", {"start": v(19.87, 6.8) * mm, "end": v(18.77, 6.91) * mm});
            skLineSegment(sketch, "E255", {"start": v(18.77, 6.91) * mm, "end": v(17.94, 6.73) * mm});
            skArc(sketch, "E256", {"start": v(17.6, 6.91) * mm, "mid": v(17.73, 6.76) * mm, "end": v(17.94, 6.73) * mm});
            skLineSegment(sketch, "E257", {"start": v(18.56, 9.83) * mm, "end": v(17.45, 9.76) * mm});
            skLineSegment(sketch, "E258", {"start": v(17.45, 9.76) * mm, "end": v(16.66, 9.45) * mm});
            skArc(sketch, "E259", {"start": v(16.3, 9.58) * mm, "mid": v(16.45, 9.45) * mm, "end": v(16.66, 9.45) * mm});
            skLineSegment(sketch, "E260", {"start": v(16.8, 12.61) * mm, "end": v(15.71, 12.37) * mm});
            skLineSegment(sketch, "E261", {"start": v(15.71, 12.37) * mm, "end": v(14.98, 11.94) * mm});
            skArc(sketch, "E262", {"start": v(14.6, 12) * mm, "mid": v(14.77, 11.9) * mm, "end": v(14.98, 11.94) * mm});
            skLineSegment(sketch, "E263", {"start": v(14.61, 15.08) * mm, "end": v(13.58, 14.68) * mm});
            skLineSegment(sketch, "E264", {"start": v(13.58, 14.68) * mm, "end": v(12.93, 14.14) * mm});
            skArc(sketch, "E265", {"start": v(12.54, 14.14) * mm, "mid": v(12.73, 14.07) * mm, "end": v(12.93, 14.14) * mm});
            skLineSegment(sketch, "E266", {"start": v(12.07, 17.18) * mm, "end": v(11.12, 16.62) * mm});
            skLineSegment(sketch, "E267", {"start": v(11.12, 16.62) * mm, "end": v(10.56, 15.98) * mm});
            skArc(sketch, "E268", {"start": v(10.17, 15.93) * mm, "mid": v(10.37, 15.89) * mm, "end": v(10.56, 15.98) * mm});
            skLineSegment(sketch, "E269", {"start": v(9.24, 18.86) * mm, "end": v(8.38, 18.16) * mm});
            skLineSegment(sketch, "E270", {"start": v(8.38, 18.16) * mm, "end": v(7.93, 17.44) * mm});
            skArc(sketch, "E271", {"start": v(7.55, 17.33) * mm, "mid": v(7.76, 17.31) * mm, "end": v(7.93, 17.44) * mm});
            skLineSegment(sketch, "E272", {"start": v(6.17, 20.07) * mm, "end": v(5.44, 19.25) * mm});
            skLineSegment(sketch, "E273", {"start": v(5.44, 19.25) * mm, "end": v(5.1, 18.46) * mm});
            skArc(sketch, "E274", {"start": v(4.75, 18.3) * mm, "mid": v(4.96, 18.31) * mm, "end": v(5.1, 18.46) * mm});
            skLineSegment(sketch, "E275", {"start": v(2.96, 20.8) * mm, "end": v(2.36, 19.86) * mm});
            skLineSegment(sketch, "E276", {"start": v(2.36, 19.86) * mm, "end": v(2.15, 19.04) * mm});
            skArc(sketch, "E277", {"start": v(1.83, 18.81) * mm, "mid": v(2.03, 18.86) * mm, "end": v(2.15, 19.04) * mm});
            skLineSegment(sketch, "E278", {"start": v(-0.33, 21) * mm, "end": v(-0.78, 19.98) * mm});
            skLineSegment(sketch, "E279", {"start": v(-0.78, 19.98) * mm, "end": v(-0.86, 19.14) * mm});
            skArc(sketch, "E280", {"start": v(-1.14, 18.87) * mm, "mid": v(-0.95, 18.95) * mm, "end": v(-0.86, 19.14) * mm});
            skLineSegment(sketch, "E281", {"start": v(-3.61, 20.69) * mm, "end": v(-3.9, 19.62) * mm});
            skLineSegment(sketch, "E282", {"start": v(-3.9, 19.62) * mm, "end": v(-3.84, 18.77) * mm});
            skArc(sketch, "E283", {"start": v(-4.07, 18.46) * mm, "mid": v(-3.9, 18.57) * mm, "end": v(-3.84, 18.77) * mm});
            skLineSegment(sketch, "E284", {"start": v(-6.8, 19.87) * mm, "end": v(-6.91, 18.77) * mm});
            skLineSegment(sketch, "E285", {"start": v(-6.91, 18.77) * mm, "end": v(-6.73, 17.94) * mm});
            skArc(sketch, "E286", {"start": v(-6.91, 17.6) * mm, "mid": v(-6.76, 17.73) * mm, "end": v(-6.73, 17.94) * mm});
            skLineSegment(sketch, "E287", {"start": v(-9.83, 18.56) * mm, "end": v(-9.76, 17.45) * mm});
            skLineSegment(sketch, "E288", {"start": v(-9.76, 17.45) * mm, "end": v(-9.45, 16.66) * mm});
            skArc(sketch, "E289", {"start": v(-9.58, 16.3) * mm, "mid": v(-9.45, 16.45) * mm, "end": v(-9.45, 16.66) * mm});
            skLineSegment(sketch, "E290", {"start": v(-12.61, 16.8) * mm, "end": v(-12.37, 15.71) * mm});
            skLineSegment(sketch, "E291", {"start": v(-12.37, 15.71) * mm, "end": v(-11.94, 14.98) * mm});
            skArc(sketch, "E292", {"start": v(-12, 14.6) * mm, "mid": v(-11.9, 14.77) * mm, "end": v(-11.94, 14.98) * mm});
            skLineSegment(sketch, "E293", {"start": v(-15.08, 14.61) * mm, "end": v(-14.68, 13.58) * mm});
            skLineSegment(sketch, "E294", {"start": v(-14.68, 13.58) * mm, "end": v(-14.14, 12.93) * mm});
            skArc(sketch, "E295", {"start": v(-14.14, 12.54) * mm, "mid": v(-14.07, 12.73) * mm, "end": v(-14.14, 12.93) * mm});
            skLineSegment(sketch, "E296", {"start": v(-17.18, 12.07) * mm, "end": v(-16.62, 11.12) * mm});
            skLineSegment(sketch, "E297", {"start": v(-16.62, 11.12) * mm, "end": v(-15.98, 10.56) * mm});
            skArc(sketch, "E298", {"start": v(-15.93, 10.17) * mm, "mid": v(-15.89, 10.37) * mm, "end": v(-15.98, 10.56) * mm});
            skLineSegment(sketch, "E299", {"start": v(-18.86, 9.24) * mm, "end": v(-18.16, 8.38) * mm});
            skLineSegment(sketch, "E300", {"start": v(-18.16, 8.38) * mm, "end": v(-17.44, 7.93) * mm});
            skArc(sketch, "E301", {"start": v(-17.33, 7.55) * mm, "mid": v(-17.31, 7.76) * mm, "end": v(-17.44, 7.93) * mm});
            skLineSegment(sketch, "E302", {"start": v(-20.07, 6.17) * mm, "end": v(-19.25, 5.44) * mm});
            skLineSegment(sketch, "E303", {"start": v(-19.25, 5.44) * mm, "end": v(-18.46, 5.1) * mm});
            skArc(sketch, "E304", {"start": v(-18.3, 4.75) * mm, "mid": v(-18.31, 4.96) * mm, "end": v(-18.46, 5.1) * mm});
            skLineSegment(sketch, "E305", {"start": v(-20.8, 2.96) * mm, "end": v(-19.86, 2.36) * mm});
            skLineSegment(sketch, "E306", {"start": v(-19.86, 2.36) * mm, "end": v(-19.04, 2.15) * mm});
            skArc(sketch, "E307", {"start": v(-18.81, 1.83) * mm, "mid": v(-18.86, 2.03) * mm, "end": v(-19.04, 2.15) * mm});
            skArc(sketch, "E308", {"start": v(21, 0) * mm, "mid": v(21, 0.17) * mm, "end": v(21, 0.33) * mm});
            skArc(sketch, "E309", {"start": v(20.8, 2.96) * mm, "mid": v(20.74, 3.29) * mm, "end": v(20.69, 3.61) * mm});
            skArc(sketch, "E310", {"start": v(20.07, 6.17) * mm, "mid": v(19.97, 6.49) * mm, "end": v(19.87, 6.8) * mm});
            skArc(sketch, "E311", {"start": v(18.86, 9.24) * mm, "mid": v(18.71, 9.53) * mm, "end": v(18.56, 9.83) * mm});
            skArc(sketch, "E312", {"start": v(17.18, 12.07) * mm, "mid": v(16.99, 12.34) * mm, "end": v(16.8, 12.61) * mm});
            skArc(sketch, "E313", {"start": v(15.08, 14.61) * mm, "mid": v(14.85, 14.85) * mm, "end": v(14.61, 15.08) * mm});
            skArc(sketch, "E314", {"start": v(12.61, 16.8) * mm, "mid": v(12.34, 16.99) * mm, "end": v(12.07, 17.18) * mm});
            skArc(sketch, "E315", {"start": v(9.83, 18.56) * mm, "mid": v(9.53, 18.71) * mm, "end": v(9.24, 18.86) * mm});
            skArc(sketch, "E316", {"start": v(6.8, 19.87) * mm, "mid": v(6.49, 19.97) * mm, "end": v(6.17, 20.07) * mm});
            skArc(sketch, "E317", {"start": v(3.61, 20.69) * mm, "mid": v(3.29, 20.74) * mm, "end": v(2.96, 20.8) * mm});
            skArc(sketch, "E318", {"start": v(0.33, 21) * mm, "mid": v(0, 21) * mm, "end": v(-0.33, 21) * mm});
            skArc(sketch, "E319", {"start": v(-2.96, 20.8) * mm, "mid": v(-3.29, 20.74) * mm, "end": v(-3.61, 20.69) * mm});
            skArc(sketch, "E320", {"start": v(-6.17, 20.07) * mm, "mid": v(-6.49, 19.97) * mm, "end": v(-6.8, 19.87) * mm});
            skArc(sketch, "E321", {"start": v(-9.24, 18.86) * mm, "mid": v(-9.53, 18.71) * mm, "end": v(-9.83, 18.56) * mm});
            skArc(sketch, "E322", {"start": v(-12.07, 17.18) * mm, "mid": v(-12.34, 16.99) * mm, "end": v(-12.61, 16.8) * mm});
            skArc(sketch, "E323", {"start": v(-14.61, 15.08) * mm, "mid": v(-14.85, 14.85) * mm, "end": v(-15.08, 14.61) * mm});
            skArc(sketch, "E324", {"start": v(-16.8, 12.61) * mm, "mid": v(-16.99, 12.34) * mm, "end": v(-17.18, 12.07) * mm});
            skArc(sketch, "E325", {"start": v(-18.56, 9.83) * mm, "mid": v(-18.71, 9.53) * mm, "end": v(-18.86, 9.24) * mm});
            skArc(sketch, "E326", {"start": v(-19.87, 6.8) * mm, "mid": v(-19.97, 6.49) * mm, "end": v(-20.07, 6.17) * mm});
            skArc(sketch, "E327", {"start": v(-20.69, 3.61) * mm, "mid": v(-20.74, 3.29) * mm, "end": v(-20.8, 2.96) * mm});
            skArc(sketch, "E328", {"start": v(-21, 0.33) * mm, "mid": v(-21, 0.17) * mm, "end": v(-21, 0) * mm});
            skArc(sketch, "E329", {"start": v(-20.8, -2.96) * mm, "mid": v(-20.74, -3.29) * mm, "end": v(-20.69, -3.61) * mm});
            skArc(sketch, "E330", {"start": v(-20.07, -6.17) * mm, "mid": v(-19.97, -6.49) * mm, "end": v(-19.87, -6.8) * mm});
            skArc(sketch, "E331", {"start": v(-18.86, -9.24) * mm, "mid": v(-18.71, -9.53) * mm, "end": v(-18.56, -9.83) * mm});
            skArc(sketch, "E332", {"start": v(-17.18, -12.07) * mm, "mid": v(-16.99, -12.34) * mm, "end": v(-16.8, -12.61) * mm});
            skArc(sketch, "E333", {"start": v(-15.08, -14.61) * mm, "mid": v(-14.85, -14.85) * mm, "end": v(-14.61, -15.08) * mm});
            skArc(sketch, "E334", {"start": v(-12.61, -16.8) * mm, "mid": v(-12.34, -16.99) * mm, "end": v(-12.07, -17.18) * mm});
            skArc(sketch, "E335", {"start": v(-9.83, -18.56) * mm, "mid": v(-9.53, -18.71) * mm, "end": v(-9.24, -18.86) * mm});
            skArc(sketch, "E336", {"start": v(-6.8, -19.87) * mm, "mid": v(-6.49, -19.97) * mm, "end": v(-6.17, -20.07) * mm});
            skArc(sketch, "E337", {"start": v(-3.61, -20.69) * mm, "mid": v(-3.29, -20.74) * mm, "end": v(-2.96, -20.8) * mm});
            skArc(sketch, "E338", {"start": v(-0.33, -21) * mm, "mid": v(0, -21) * mm, "end": v(0.33, -21) * mm});
            skArc(sketch, "E339", {"start": v(2.96, -20.8) * mm, "mid": v(3.29, -20.74) * mm, "end": v(3.61, -20.69) * mm});
            skArc(sketch, "E340", {"start": v(6.17, -20.07) * mm, "mid": v(6.49, -19.97) * mm, "end": v(6.8, -19.87) * mm});
            skArc(sketch, "E341", {"start": v(9.24, -18.86) * mm, "mid": v(9.53, -18.71) * mm, "end": v(9.83, -18.56) * mm});
            skArc(sketch, "E342", {"start": v(12.07, -17.18) * mm, "mid": v(12.34, -16.99) * mm, "end": v(12.61, -16.8) * mm});
            skArc(sketch, "E343", {"start": v(14.61, -15.08) * mm, "mid": v(14.85, -14.85) * mm, "end": v(15.08, -14.61) * mm});
            skArc(sketch, "E344", {"start": v(16.8, -12.61) * mm, "mid": v(16.99, -12.34) * mm, "end": v(17.18, -12.07) * mm});
            skArc(sketch, "E345", {"start": v(18.56, -9.83) * mm, "mid": v(18.71, -9.53) * mm, "end": v(18.86, -9.24) * mm});
            skArc(sketch, "E346", {"start": v(19.87, -6.8) * mm, "mid": v(19.97, -6.49) * mm, "end": v(20.07, -6.17) * mm});
            skArc(sketch, "E347", {"start": v(20.69, -3.61) * mm, "mid": v(20.74, -3.29) * mm, "end": v(20.8, -2.96) * mm});
            skArc(sketch, "E348", {"start": v(0, 5) * mm, "mid": v(-5, 0) * mm, "end": v(0, -5) * mm});
            skArc(sketch, "E349", {"start": v(12.5, 0) * mm, "mid": v(0, 12.5) * mm, "end": v(-12.5, 0) * mm});
            skSolve(sketch);
        }
        {
            var Q0;
            {var subQ3=sQuery(id+"F4.wireOp",EDGE,"E42");Q0=makeQuery(id+"F4.imprint","IMPRINT",FACE,{"disambiguationData":[TD([[makeQuery(id+"F4.imprint","IMPRINT",EDGE,{"derivedFrom":subQ3}),-1.0]])]});}
            var Q1;
            Q1=makeQuery(id+"F4.imprint","IMPRINT",FACE,{"disambiguationData":[TD([[makeQuery(id+"F4.imprint","IMPRINT",EDGE,{"derivedFrom":sQuery(id+"F4.wireOp",EDGE,"E52")}),-1.0]])]});
            var Q2;
            Q2=makeQuery(id+"F4.imprint","IMPRINT",FACE,{"disambiguationData":[TD([[makeQuery(id+"F4.imprint","IMPRINT",EDGE,{"derivedFrom":sQuery(id+"F4.wireOp",EDGE,"E121")}),-1.0]])]});
            var Q3;
            {var subQ6=sQuery(id+"F4.wireOp",EDGE,"E113");Q3=makeQuery(id+"F4.imprint","IMPRINT",FACE,{"disambiguationData":[TD([[makeQuery(id+"F4.imprint","IMPRINT",EDGE,{"derivedFrom":subQ6}),-1.0]])]});}
            var Q4;
            Q4=makeQuery(id+"F4.imprint","IMPRINT",FACE,{"disambiguationData":[TD([[makeQuery(id+"F4.imprint","IMPRINT",EDGE,{"derivedFrom":sQuery(id+"F4.wireOp",EDGE,"E24")}),1.0]])]});
            var Q5;
            Q5=makeQuery(id+"F4.imprint","IMPRINT",FACE,{"disambiguationData":[TD([[makeQuery(id+"F4.imprint","IMPRINT",EDGE,{"derivedFrom":sQuery(id+"F4.wireOp",EDGE,"E25")}),1.0]])]});
            extrude(context, id + "F5", {"entities" : qUnion([Q0, Q1, Q2, Q3, Q4, Q5]), "depth" : 9 * mm});
        }
        {
            var Q0;
            Q0=makeQuery(id+"F5.opExtrude","CAP_FACE",FACE,{"disambiguationData":[OSD([sQuery(id+"F4.wireOp",EDGE,"E24"),sQuery(id+"F4.wireOp",EDGE,"E26"),sQuery(id+"F4.wireOp",EDGE,"E27"),sQuery(id+"F4.wireOp",EDGE,"E28"),sQuery(id+"F4.wireOp",EDGE,"E29"),sQuery(id+"F4.wireOp",EDGE,"E30"),sQuery(id+"F4.wireOp",EDGE,"E31"),sQuery(id+"F4.wireOp",EDGE,"E32"),sQuery(id+"F4.wireOp",EDGE,"E33"),sQuery(id+"F4.wireOp",EDGE,"E34"),sQuery(id+"F4.wireOp",EDGE,"E35"),sQuery(id+"F4.wireOp",EDGE,"E36"),sQuery(id+"F4.wireOp",EDGE,"E37"),sQuery(id+"F4.wireOp",EDGE,"E38"),sQuery(id+"F4.wireOp",EDGE,"E39"),sQuery(id+"F4.wireOp",EDGE,"E40"),sQuery(id+"F4.wireOp",EDGE,"E41"),sQuery(id+"F4.wireOp",EDGE,"E42"),sQuery(id+"F4.wireOp",EDGE,"E43"),sQuery(id+"F4.wireOp",EDGE,"E44"),sQuery(id+"F4.wireOp",EDGE,"E45"),sQuery(id+"F4.wireOp",EDGE,"E46"),sQuery(id+"F4.wireOp",EDGE,"E47"),sQuery(id+"F4.wireOp",EDGE,"E48"),sQuery(id+"F4.wireOp",EDGE,"E49"),sQuery(id+"F4.wireOp",EDGE,"E50"),sQuery(id+"F4.wireOp",EDGE,"E51"),sQuery(id+"F4.wireOp",EDGE,"E52"),sQuery(id+"F4.wireOp",EDGE,"E53"),sQuery(id+"F4.wireOp",EDGE,"E54"),sQuery(id+"F4.wireOp",EDGE,"E55"),sQuery(id+"F4.wireOp",EDGE,"E56"),sQuery(id+"F4.wireOp",EDGE,"E57"),sQuery(id+"F4.wireOp",EDGE,"E58"),sQuery(id+"F4.wireOp",EDGE,"E59"),sQuery(id+"F4.wireOp",EDGE,"E60"),sQuery(id+"F4.wireOp",EDGE,"E61"),sQuery(id+"F4.wireOp",EDGE,"E62"),sQuery(id+"F4.wireOp",EDGE,"E63"),sQuery(id+"F4.wireOp",EDGE,"E64"),sQuery(id+"F4.wireOp",EDGE,"E65"),sQuery(id+"F4.wireOp",EDGE,"E66"),sQuery(id+"F4.wireOp",EDGE,"E67"),sQuery(id+"F4.wireOp",EDGE,"E68"),sQuery(id+"F4.wireOp",EDGE,"E69"),sQuery(id+"F4.wireOp",EDGE,"E70"),sQuery(id+"F4.wireOp",EDGE,"E71"),sQuery(id+"F4.wireOp",EDGE,"E72"),sQuery(id+"F4.wireOp",EDGE,"E73"),sQuery(id+"F4.wireOp",EDGE,"E74"),sQuery(id+"F4.wireOp",EDGE,"E75"),sQuery(id+"F4.wireOp",EDGE,"E76"),sQuery(id+"F4.wireOp",EDGE,"E77"),sQuery(id+"F4.wireOp",EDGE,"E78"),sQuery(id+"F4.wireOp",EDGE,"E79"),sQuery(id+"F4.wireOp",EDGE,"E80"),sQuery(id+"F4.wireOp",EDGE,"E81"),sQuery(id+"F4.wireOp",EDGE,"E82"),sQuery(id+"F4.wireOp",EDGE,"E83"),sQuery(id+"F4.wireOp",EDGE,"E84"),sQuery(id+"F4.wireOp",EDGE,"E85"),sQuery(id+"F4.wireOp",EDGE,"E86"),sQuery(id+"F4.wireOp",EDGE,"E87"),sQuery(id+"F4.wireOp",EDGE,"E88"),sQuery(id+"F4.wireOp",EDGE,"E89"),sQuery(id+"F4.wireOp",EDGE,"E90"),sQuery(id+"F4.wireOp",EDGE,"E91"),sQuery(id+"F4.wireOp",EDGE,"E92"),sQuery(id+"F4.wireOp",EDGE,"E93"),sQuery(id+"F4.wireOp",EDGE,"E94"),sQuery(id+"F4.wireOp",EDGE,"E95"),sQuery(id+"F4.wireOp",EDGE,"E96"),sQuery(id+"F4.wireOp",EDGE,"E97"),sQuery(id+"F4.wireOp",EDGE,"E98"),sQuery(id+"F4.wireOp",EDGE,"E99"),sQuery(id+"F4.wireOp",EDGE,"E100"),sQuery(id+"F4.wireOp",EDGE,"E101"),sQuery(id+"F4.wireOp",EDGE,"E102"),sQuery(id+"F4.wireOp",EDGE,"E103"),sQuery(id+"F4.wireOp",EDGE,"E104"),sQuery(id+"F4.wireOp",EDGE,"E105"),sQuery(id+"F4.wireOp",EDGE,"E106"),sQuery(id+"F4.wireOp",EDGE,"E107"),sQuery(id+"F4.wireOp",EDGE,"E108"),sQuery(id+"F4.wireOp",EDGE,"E109"),sQuery(id+"F4.wireOp",EDGE,"E110"),sQuery(id+"F4.wireOp",EDGE,"E111"),sQuery(id+"F4.wireOp",EDGE,"E112"),sQuery(id+"F4.wireOp",EDGE,"E113"),sQuery(id+"F4.wireOp",EDGE,"E114"),sQuery(id+"F4.wireOp",EDGE,"E115"),sQuery(id+"F4.wireOp",EDGE,"E116"),sQuery(id+"F4.wireOp",EDGE,"E117"),sQuery(id+"F4.wireOp",EDGE,"E118"),sQuery(id+"F4.wireOp",EDGE,"E119"),sQuery(id+"F4.wireOp",EDGE,"E120"),sQuery(id+"F4.wireOp",EDGE,"E121"),sQuery(id+"F4.wireOp",EDGE,"E122"),sQuery(id+"F4.wireOp",EDGE,"E123"),sQuery(id+"F4.wireOp",EDGE,"E124"),sQuery(id+"F4.wireOp",EDGE,"E125"),sQuery(id+"F4.wireOp",EDGE,"E126"),sQuery(id+"F4.wireOp",EDGE,"E127"),sQuery(id+"F4.wireOp",EDGE,"E128"),sQuery(id+"F4.wireOp",EDGE,"E129"),sQuery(id+"F4.wireOp",EDGE,"E130"),sQuery(id+"F4.wireOp",EDGE,"E131"),sQuery(id+"F4.wireOp",EDGE,"E132"),sQuery(id+"F4.wireOp",EDGE,"E133"),sQuery(id+"F4.wireOp",EDGE,"E134"),sQuery(id+"F4.wireOp",EDGE,"E135"),sQuery(id+"F4.wireOp",EDGE,"E136"),sQuery(id+"F4.wireOp",EDGE,"E137"),sQuery(id+"F4.wireOp",EDGE,"E138"),sQuery(id+"F4.wireOp",EDGE,"E139"),sQuery(id+"F4.wireOp",EDGE,"E140"),sQuery(id+"F4.wireOp",EDGE,"E141"),sQuery(id+"F4.wireOp",EDGE,"E142"),sQuery(id+"F4.wireOp",EDGE,"E143"),sQuery(id+"F4.wireOp",EDGE,"E144"),sQuery(id+"F4.wireOp",EDGE,"E145"),sQuery(id+"F4.wireOp",EDGE,"E146"),sQuery(id+"F4.wireOp",EDGE,"E147"),sQuery(id+"F4.wireOp",EDGE,"E148"),sQuery(id+"F4.wireOp",EDGE,"E149"),sQuery(id+"F4.wireOp",EDGE,"E150"),sQuery(id+"F4.wireOp",EDGE,"E151"),sQuery(id+"F4.wireOp",EDGE,"E152"),sQuery(id+"F4.wireOp",EDGE,"E153"),sQuery(id+"F4.wireOp",EDGE,"E154"),sQuery(id+"F4.wireOp",EDGE,"E155"),sQuery(id+"F4.wireOp",EDGE,"E156"),sQuery(id+"F4.wireOp",EDGE,"E157"),sQuery(id+"F4.wireOp",EDGE,"E158"),sQuery(id+"F4.wireOp",EDGE,"E159"),sQuery(id+"F4.wireOp",EDGE,"E160"),sQuery(id+"F4.wireOp",EDGE,"E161"),sQuery(id+"F4.wireOp",EDGE,"E162"),sQuery(id+"F4.wireOp",EDGE,"E163"),sQuery(id+"F4.wireOp",EDGE,"E164"),sQuery(id+"F4.wireOp",EDGE,"E165"),sQuery(id+"F4.wireOp",EDGE,"E166"),sQuery(id+"F4.wireOp",EDGE,"E167"),sQuery(id+"F4.wireOp",EDGE,"E168"),sQuery(id+"F4.wireOp",EDGE,"E169"),sQuery(id+"F4.wireOp",EDGE,"E170"),sQuery(id+"F4.wireOp",EDGE,"E171"),sQuery(id+"F4.wireOp",EDGE,"E172"),sQuery(id+"F4.wireOp",EDGE,"E173"),sQuery(id+"F4.wireOp",EDGE,"E174"),sQuery(id+"F4.wireOp",EDGE,"E175"),sQuery(id+"F4.wireOp",EDGE,"E176"),sQuery(id+"F4.wireOp",EDGE,"E177"),sQuery(id+"F4.wireOp",EDGE,"E178"),sQuery(id+"F4.wireOp",EDGE,"E179"),sQuery(id+"F4.wireOp",EDGE,"E180"),sQuery(id+"F4.wireOp",EDGE,"E181"),sQuery(id+"F4.wireOp",EDGE,"E182"),sQuery(id+"F4.wireOp",EDGE,"E183"),sQuery(id+"F4.wireOp",EDGE,"E184"),sQuery(id+"F4.wireOp",EDGE,"E185"),sQuery(id+"F4.wireOp",EDGE,"E186"),sQuery(id+"F4.wireOp",EDGE,"E187"),sQuery(id+"F4.wireOp",EDGE,"E188"),sQuery(id+"F4.wireOp",EDGE,"E189"),sQuery(id+"F4.wireOp",EDGE,"E190"),sQuery(id+"F4.wireOp",EDGE,"E191"),sQuery(id+"F4.wireOp",EDGE,"E192"),sQuery(id+"F4.wireOp",EDGE,"E193"),sQuery(id+"F4.wireOp",EDGE,"E194"),sQuery(id+"F4.wireOp",EDGE,"E195"),sQuery(id+"F4.wireOp",EDGE,"E196"),sQuery(id+"F4.wireOp",EDGE,"E197"),sQuery(id+"F4.wireOp",EDGE,"E198"),sQuery(id+"F4.wireOp",EDGE,"E199"),sQuery(id+"F4.wireOp",EDGE,"E200"),sQuery(id+"F4.wireOp",EDGE,"E201"),sQuery(id+"F4.wireOp",EDGE,"E202"),sQuery(id+"F4.wireOp",EDGE,"E203"),sQuery(id+"F4.wireOp",EDGE,"E204"),sQuery(id+"F4.wireOp",EDGE,"E205"),sQuery(id+"F4.wireOp",EDGE,"E206"),sQuery(id+"F4.wireOp",EDGE,"E207"),sQuery(id+"F4.wireOp",EDGE,"E208"),sQuery(id+"F4.wireOp",EDGE,"E209"),sQuery(id+"F4.wireOp",EDGE,"E210"),sQuery(id+"F4.wireOp",EDGE,"E211"),sQuery(id+"F4.wireOp",EDGE,"E212"),sQuery(id+"F4.wireOp",EDGE,"E213"),sQuery(id+"F4.wireOp",EDGE,"E214"),sQuery(id+"F4.wireOp",EDGE,"E215"),sQuery(id+"F4.wireOp",EDGE,"E216"),sQuery(id+"F4.wireOp",EDGE,"E217"),sQuery(id+"F4.wireOp",EDGE,"E218"),sQuery(id+"F4.wireOp",EDGE,"E219"),sQuery(id+"F4.wireOp",EDGE,"E220"),sQuery(id+"F4.wireOp",EDGE,"E221"),sQuery(id+"F4.wireOp",EDGE,"E222"),sQuery(id+"F4.wireOp",EDGE,"E223"),sQuery(id+"F4.wireOp",EDGE,"E224"),sQuery(id+"F4.wireOp",EDGE,"E225"),sQuery(id+"F4.wireOp",EDGE,"E226"),sQuery(id+"F4.wireOp",EDGE,"E227"),sQuery(id+"F4.wireOp",EDGE,"E228"),sQuery(id+"F4.wireOp",EDGE,"E229"),sQuery(id+"F4.wireOp",EDGE,"E230"),sQuery(id+"F4.wireOp",EDGE,"E231"),sQuery(id+"F4.wireOp",EDGE,"E232"),sQuery(id+"F4.wireOp",EDGE,"E233"),sQuery(id+"F4.wireOp",EDGE,"E234"),sQuery(id+"F4.wireOp",EDGE,"E235"),sQuery(id+"F4.wireOp",EDGE,"E236"),sQuery(id+"F4.wireOp",EDGE,"E237"),sQuery(id+"F4.wireOp",EDGE,"E238"),sQuery(id+"F4.wireOp",EDGE,"E239"),sQuery(id+"F4.wireOp",EDGE,"E240"),sQuery(id+"F4.wireOp",EDGE,"E241"),sQuery(id+"F4.wireOp",EDGE,"E242"),sQuery(id+"F4.wireOp",EDGE,"E243"),sQuery(id+"F4.wireOp",EDGE,"E244"),sQuery(id+"F4.wireOp",EDGE,"E245"),sQuery(id+"F4.wireOp",EDGE,"E246"),sQuery(id+"F4.wireOp",EDGE,"E247"),sQuery(id+"F4.wireOp",EDGE,"E248"),sQuery(id+"F4.wireOp",EDGE,"E249"),sQuery(id+"F4.wireOp",EDGE,"E250"),sQuery(id+"F4.wireOp",EDGE,"E251"),sQuery(id+"F4.wireOp",EDGE,"E252"),sQuery(id+"F4.wireOp",EDGE,"E253"),sQuery(id+"F4.wireOp",EDGE,"E254"),sQuery(id+"F4.wireOp",EDGE,"E255"),sQuery(id+"F4.wireOp",EDGE,"E256"),sQuery(id+"F4.wireOp",EDGE,"E257"),sQuery(id+"F4.wireOp",EDGE,"E258"),sQuery(id+"F4.wireOp",EDGE,"E259"),sQuery(id+"F4.wireOp",EDGE,"E260"),sQuery(id+"F4.wireOp",EDGE,"E261"),sQuery(id+"F4.wireOp",EDGE,"E262"),sQuery(id+"F4.wireOp",EDGE,"E263"),sQuery(id+"F4.wireOp",EDGE,"E264"),sQuery(id+"F4.wireOp",EDGE,"E265"),sQuery(id+"F4.wireOp",EDGE,"E266"),sQuery(id+"F4.wireOp",EDGE,"E267"),sQuery(id+"F4.wireOp",EDGE,"E268"),sQuery(id+"F4.wireOp",EDGE,"E269"),sQuery(id+"F4.wireOp",EDGE,"E270"),sQuery(id+"F4.wireOp",EDGE,"E271"),sQuery(id+"F4.wireOp",EDGE,"E272"),sQuery(id+"F4.wireOp",EDGE,"E273"),sQuery(id+"F4.wireOp",EDGE,"E274"),sQuery(id+"F4.wireOp",EDGE,"E275"),sQuery(id+"F4.wireOp",EDGE,"E276"),sQuery(id+"F4.wireOp",EDGE,"E277"),sQuery(id+"F4.wireOp",EDGE,"E278"),sQuery(id+"F4.wireOp",EDGE,"E279"),sQuery(id+"F4.wireOp",EDGE,"E280"),sQuery(id+"F4.wireOp",EDGE,"E281"),sQuery(id+"F4.wireOp",EDGE,"E282"),sQuery(id+"F4.wireOp",EDGE,"E283"),sQuery(id+"F4.wireOp",EDGE,"E284"),sQuery(id+"F4.wireOp",EDGE,"E285"),sQuery(id+"F4.wireOp",EDGE,"E286"),sQuery(id+"F4.wireOp",EDGE,"E287"),sQuery(id+"F4.wireOp",EDGE,"E288"),sQuery(id+"F4.wireOp",EDGE,"E289"),sQuery(id+"F4.wireOp",EDGE,"E290"),sQuery(id+"F4.wireOp",EDGE,"E291"),sQuery(id+"F4.wireOp",EDGE,"E292"),sQuery(id+"F4.wireOp",EDGE,"E293"),sQuery(id+"F4.wireOp",EDGE,"E294"),sQuery(id+"F4.wireOp",EDGE,"E295"),sQuery(id+"F4.wireOp",EDGE,"E296"),sQuery(id+"F4.wireOp",EDGE,"E297"),sQuery(id+"F4.wireOp",EDGE,"E298"),sQuery(id+"F4.wireOp",EDGE,"E299"),sQuery(id+"F4.wireOp",EDGE,"E300"),sQuery(id+"F4.wireOp",EDGE,"E301"),sQuery(id+"F4.wireOp",EDGE,"E302"),sQuery(id+"F4.wireOp",EDGE,"E303"),sQuery(id+"F4.wireOp",EDGE,"E304"),sQuery(id+"F4.wireOp",EDGE,"E305"),sQuery(id+"F4.wireOp",EDGE,"E306"),sQuery(id+"F4.wireOp",EDGE,"E307"),sQuery(id+"F4.wireOp",EDGE,"E308"),sQuery(id+"F4.wireOp",EDGE,"E309"),sQuery(id+"F4.wireOp",EDGE,"E310"),sQuery(id+"F4.wireOp",EDGE,"E311"),sQuery(id+"F4.wireOp",EDGE,"E312"),sQuery(id+"F4.wireOp",EDGE,"E313"),sQuery(id+"F4.wireOp",EDGE,"E314"),sQuery(id+"F4.wireOp",EDGE,"E315"),sQuery(id+"F4.wireOp",EDGE,"E316"),sQuery(id+"F4.wireOp",EDGE,"E317"),sQuery(id+"F4.wireOp",EDGE,"E318"),sQuery(id+"F4.wireOp",EDGE,"E319"),sQuery(id+"F4.wireOp",EDGE,"E320"),sQuery(id+"F4.wireOp",EDGE,"E321"),sQuery(id+"F4.wireOp",EDGE,"E322"),sQuery(id+"F4.wireOp",EDGE,"E323"),sQuery(id+"F4.wireOp",EDGE,"E324"),sQuery(id+"F4.wireOp",EDGE,"E325"),sQuery(id+"F4.wireOp",EDGE,"E326"),sQuery(id+"F4.wireOp",EDGE,"E327"),sQuery(id+"F4.wireOp",EDGE,"E328"),sQuery(id+"F4.wireOp",EDGE,"E329"),sQuery(id+"F4.wireOp",EDGE,"E330"),sQuery(id+"F4.wireOp",EDGE,"E331"),sQuery(id+"F4.wireOp",EDGE,"E332"),sQuery(id+"F4.wireOp",EDGE,"E333"),sQuery(id+"F4.wireOp",EDGE,"E334"),sQuery(id+"F4.wireOp",EDGE,"E335"),sQuery(id+"F4.wireOp",EDGE,"E336"),sQuery(id+"F4.wireOp",EDGE,"E337"),sQuery(id+"F4.wireOp",EDGE,"E338"),sQuery(id+"F4.wireOp",EDGE,"E339"),sQuery(id+"F4.wireOp",EDGE,"E340"),sQuery(id+"F4.wireOp",EDGE,"E341"),sQuery(id+"F4.wireOp",EDGE,"E342"),sQuery(id+"F4.wireOp",EDGE,"E343"),sQuery(id+"F4.wireOp",EDGE,"E344"),sQuery(id+"F4.wireOp",EDGE,"E345"),sQuery(id+"F4.wireOp",EDGE,"E346"),sQuery(id+"F4.wireOp",EDGE,"E347"),sQuery(id+"F4.wireOp",EDGE,"E348")])],"isStart":false});
            var sketch = newSketch(context, id + "F6", { "sketchPlane" : qUnion([Q0])});
            skCircle(sketch, "E350", {"center": v(0, 0) * mm, "radius": 9.05 * mm});
            skSolve(sketch);
        }
        {
            var Q0;
            Q0=makeQuery(id+"F6.imprint","IMPRINT",FACE,{"disambiguationData":[TD([[makeQuery(id+"F6.imprint","IMPRINT",EDGE,{"derivedFrom":sQuery(id+"F6.wireOp",EDGE,"E350")}),1.0]])]});
            extrude(context, id + "F7", {"entities" : qUnion([Q0]), "operationType" : NewBodyOperationType.REMOVE, "endBound" : BoundingType.THROUGH_ALL, "oppositeDirection" : true, "depth" : 25 * mm});
        }
        {
            var Q0;
            Q0=makeQuery(id+"F1.opExtrude","SWEPT_BODY",BODY,{"disambiguationData":[OSD([sQuery(id+"F0.wireOp",EDGE,"E11.0.startCap"),sQuery(id+"F0.wireOp",EDGE,"E11.0.endCap"),sQuery(id+"F0.wireOp",EDGE,"E11.0.left"),sQuery(id+"F0.wireOp",EDGE,"E11.0.right"),sQuery(id+"F0.wireOp",EDGE,"E12.0.startCap"),sQuery(id+"F0.wireOp",EDGE,"E12.0.endCap"),sQuery(id+"F0.wireOp",EDGE,"E12.0.left"),sQuery(id+"F0.wireOp",EDGE,"E12.0.right"),sQuery(id+"F0.wireOp",EDGE,"E13.trimOffspring"),sQuery(id+"F0.wireOp",EDGE,"E14.trimOffspring"),sQuery(id+"F0.wireOp",EDGE,"E15.trimOffspring"),sQuery(id+"F0.wireOp",EDGE,"E16.trimOffspring"),sQuery(id+"F0.wireOp",EDGE,"E17.filletArc"),sQuery(id+"F0.wireOp",EDGE,"E18.filletArc"),sQuery(id+"F0.wireOp",EDGE,"E19.filletArc"),sQuery(id+"F0.wireOp",EDGE,"E20.filletArc"),sQuery(id+"F0.wireOp",EDGE,"E21")])]});
            var Q1;
            Q1=qCreatedBy(makeId("Origin.pointOp"),VERTEX);
            transform(context, id + "F8", {"entities" : qUnion([Q0]), "transformType" : TransformType.SCALE_UNIFORMLY, "scale" : .6, "makeCopy" : false, "scalePoint" : qUnion([Q1])});
        }
        {
            var Q0;
            Q0=makeQuery(id+"F5.opExtrude","CAP_FACE",FACE,{"disambiguationData":[OSD([sQuery(id+"F4.wireOp",EDGE,"E24"),sQuery(id+"F4.wireOp",EDGE,"E26"),sQuery(id+"F4.wireOp",EDGE,"E27"),sQuery(id+"F4.wireOp",EDGE,"E28"),sQuery(id+"F4.wireOp",EDGE,"E29"),sQuery(id+"F4.wireOp",EDGE,"E30"),sQuery(id+"F4.wireOp",EDGE,"E31"),sQuery(id+"F4.wireOp",EDGE,"E32"),sQuery(id+"F4.wireOp",EDGE,"E33"),sQuery(id+"F4.wireOp",EDGE,"E34"),sQuery(id+"F4.wireOp",EDGE,"E35"),sQuery(id+"F4.wireOp",EDGE,"E36"),sQuery(id+"F4.wireOp",EDGE,"E37"),sQuery(id+"F4.wireOp",EDGE,"E38"),sQuery(id+"F4.wireOp",EDGE,"E39"),sQuery(id+"F4.wireOp",EDGE,"E40"),sQuery(id+"F4.wireOp",EDGE,"E41"),sQuery(id+"F4.wireOp",EDGE,"E42"),sQuery(id+"F4.wireOp",EDGE,"E43"),sQuery(id+"F4.wireOp",EDGE,"E44"),sQuery(id+"F4.wireOp",EDGE,"E45"),sQuery(id+"F4.wireOp",EDGE,"E46"),sQuery(id+"F4.wireOp",EDGE,"E47"),sQuery(id+"F4.wireOp",EDGE,"E48"),sQuery(id+"F4.wireOp",EDGE,"E49"),sQuery(id+"F4.wireOp",EDGE,"E50"),sQuery(id+"F4.wireOp",EDGE,"E51"),sQuery(id+"F4.wireOp",EDGE,"E52"),sQuery(id+"F4.wireOp",EDGE,"E53"),sQuery(id+"F4.wireOp",EDGE,"E54"),sQuery(id+"F4.wireOp",EDGE,"E55"),sQuery(id+"F4.wireOp",EDGE,"E56"),sQuery(id+"F4.wireOp",EDGE,"E57"),sQuery(id+"F4.wireOp",EDGE,"E58"),sQuery(id+"F4.wireOp",EDGE,"E59"),sQuery(id+"F4.wireOp",EDGE,"E60"),sQuery(id+"F4.wireOp",EDGE,"E61"),sQuery(id+"F4.wireOp",EDGE,"E62"),sQuery(id+"F4.wireOp",EDGE,"E63"),sQuery(id+"F4.wireOp",EDGE,"E64"),sQuery(id+"F4.wireOp",EDGE,"E65"),sQuery(id+"F4.wireOp",EDGE,"E66"),sQuery(id+"F4.wireOp",EDGE,"E67"),sQuery(id+"F4.wireOp",EDGE,"E68"),sQuery(id+"F4.wireOp",EDGE,"E69"),sQuery(id+"F4.wireOp",EDGE,"E70"),sQuery(id+"F4.wireOp",EDGE,"E71"),sQuery(id+"F4.wireOp",EDGE,"E72"),sQuery(id+"F4.wireOp",EDGE,"E73"),sQuery(id+"F4.wireOp",EDGE,"E74"),sQuery(id+"F4.wireOp",EDGE,"E75"),sQuery(id+"F4.wireOp",EDGE,"E76"),sQuery(id+"F4.wireOp",EDGE,"E77"),sQuery(id+"F4.wireOp",EDGE,"E78"),sQuery(id+"F4.wireOp",EDGE,"E79"),sQuery(id+"F4.wireOp",EDGE,"E80"),sQuery(id+"F4.wireOp",EDGE,"E81"),sQuery(id+"F4.wireOp",EDGE,"E82"),sQuery(id+"F4.wireOp",EDGE,"E83"),sQuery(id+"F4.wireOp",EDGE,"E84"),sQuery(id+"F4.wireOp",EDGE,"E85"),sQuery(id+"F4.wireOp",EDGE,"E86"),sQuery(id+"F4.wireOp",EDGE,"E87"),sQuery(id+"F4.wireOp",EDGE,"E88"),sQuery(id+"F4.wireOp",EDGE,"E89"),sQuery(id+"F4.wireOp",EDGE,"E90"),sQuery(id+"F4.wireOp",EDGE,"E91"),sQuery(id+"F4.wireOp",EDGE,"E92"),sQuery(id+"F4.wireOp",EDGE,"E93"),sQuery(id+"F4.wireOp",EDGE,"E94"),sQuery(id+"F4.wireOp",EDGE,"E95"),sQuery(id+"F4.wireOp",EDGE,"E96"),sQuery(id+"F4.wireOp",EDGE,"E97"),sQuery(id+"F4.wireOp",EDGE,"E98"),sQuery(id+"F4.wireOp",EDGE,"E99"),sQuery(id+"F4.wireOp",EDGE,"E100"),sQuery(id+"F4.wireOp",EDGE,"E101"),sQuery(id+"F4.wireOp",EDGE,"E102"),sQuery(id+"F4.wireOp",EDGE,"E103"),sQuery(id+"F4.wireOp",EDGE,"E104"),sQuery(id+"F4.wireOp",EDGE,"E105"),sQuery(id+"F4.wireOp",EDGE,"E106"),sQuery(id+"F4.wireOp",EDGE,"E107"),sQuery(id+"F4.wireOp",EDGE,"E108"),sQuery(id+"F4.wireOp",EDGE,"E109"),sQuery(id+"F4.wireOp",EDGE,"E110"),sQuery(id+"F4.wireOp",EDGE,"E111"),sQuery(id+"F4.wireOp",EDGE,"E112"),sQuery(id+"F4.wireOp",EDGE,"E113"),sQuery(id+"F4.wireOp",EDGE,"E114"),sQuery(id+"F4.wireOp",EDGE,"E115"),sQuery(id+"F4.wireOp",EDGE,"E116"),sQuery(id+"F4.wireOp",EDGE,"E117"),sQuery(id+"F4.wireOp",EDGE,"E118"),sQuery(id+"F4.wireOp",EDGE,"E119"),sQuery(id+"F4.wireOp",EDGE,"E120"),sQuery(id+"F4.wireOp",EDGE,"E121"),sQuery(id+"F4.wireOp",EDGE,"E122"),sQuery(id+"F4.wireOp",EDGE,"E123"),sQuery(id+"F4.wireOp",EDGE,"E124"),sQuery(id+"F4.wireOp",EDGE,"E125"),sQuery(id+"F4.wireOp",EDGE,"E126"),sQuery(id+"F4.wireOp",EDGE,"E127"),sQuery(id+"F4.wireOp",EDGE,"E128"),sQuery(id+"F4.wireOp",EDGE,"E129"),sQuery(id+"F4.wireOp",EDGE,"E130"),sQuery(id+"F4.wireOp",EDGE,"E131"),sQuery(id+"F4.wireOp",EDGE,"E132"),sQuery(id+"F4.wireOp",EDGE,"E133"),sQuery(id+"F4.wireOp",EDGE,"E134"),sQuery(id+"F4.wireOp",EDGE,"E135"),sQuery(id+"F4.wireOp",EDGE,"E136"),sQuery(id+"F4.wireOp",EDGE,"E137"),sQuery(id+"F4.wireOp",EDGE,"E138"),sQuery(id+"F4.wireOp",EDGE,"E139"),sQuery(id+"F4.wireOp",EDGE,"E140"),sQuery(id+"F4.wireOp",EDGE,"E141"),sQuery(id+"F4.wireOp",EDGE,"E142"),sQuery(id+"F4.wireOp",EDGE,"E143"),sQuery(id+"F4.wireOp",EDGE,"E144"),sQuery(id+"F4.wireOp",EDGE,"E145"),sQuery(id+"F4.wireOp",EDGE,"E146"),sQuery(id+"F4.wireOp",EDGE,"E147"),sQuery(id+"F4.wireOp",EDGE,"E148"),sQuery(id+"F4.wireOp",EDGE,"E149"),sQuery(id+"F4.wireOp",EDGE,"E150"),sQuery(id+"F4.wireOp",EDGE,"E151"),sQuery(id+"F4.wireOp",EDGE,"E152"),sQuery(id+"F4.wireOp",EDGE,"E153"),sQuery(id+"F4.wireOp",EDGE,"E154"),sQuery(id+"F4.wireOp",EDGE,"E155"),sQuery(id+"F4.wireOp",EDGE,"E156"),sQuery(id+"F4.wireOp",EDGE,"E157"),sQuery(id+"F4.wireOp",EDGE,"E158"),sQuery(id+"F4.wireOp",EDGE,"E159"),sQuery(id+"F4.wireOp",EDGE,"E160"),sQuery(id+"F4.wireOp",EDGE,"E161"),sQuery(id+"F4.wireOp",EDGE,"E162"),sQuery(id+"F4.wireOp",EDGE,"E163"),sQuery(id+"F4.wireOp",EDGE,"E164"),sQuery(id+"F4.wireOp",EDGE,"E165"),sQuery(id+"F4.wireOp",EDGE,"E166"),sQuery(id+"F4.wireOp",EDGE,"E167"),sQuery(id+"F4.wireOp",EDGE,"E168"),sQuery(id+"F4.wireOp",EDGE,"E169"),sQuery(id+"F4.wireOp",EDGE,"E170"),sQuery(id+"F4.wireOp",EDGE,"E171"),sQuery(id+"F4.wireOp",EDGE,"E172"),sQuery(id+"F4.wireOp",EDGE,"E173"),sQuery(id+"F4.wireOp",EDGE,"E174"),sQuery(id+"F4.wireOp",EDGE,"E175"),sQuery(id+"F4.wireOp",EDGE,"E176"),sQuery(id+"F4.wireOp",EDGE,"E177"),sQuery(id+"F4.wireOp",EDGE,"E178"),sQuery(id+"F4.wireOp",EDGE,"E179"),sQuery(id+"F4.wireOp",EDGE,"E180"),sQuery(id+"F4.wireOp",EDGE,"E181"),sQuery(id+"F4.wireOp",EDGE,"E182"),sQuery(id+"F4.wireOp",EDGE,"E183"),sQuery(id+"F4.wireOp",EDGE,"E184"),sQuery(id+"F4.wireOp",EDGE,"E185"),sQuery(id+"F4.wireOp",EDGE,"E186"),sQuery(id+"F4.wireOp",EDGE,"E187"),sQuery(id+"F4.wireOp",EDGE,"E188"),sQuery(id+"F4.wireOp",EDGE,"E189"),sQuery(id+"F4.wireOp",EDGE,"E190"),sQuery(id+"F4.wireOp",EDGE,"E191"),sQuery(id+"F4.wireOp",EDGE,"E192"),sQuery(id+"F4.wireOp",EDGE,"E193"),sQuery(id+"F4.wireOp",EDGE,"E194"),sQuery(id+"F4.wireOp",EDGE,"E195"),sQuery(id+"F4.wireOp",EDGE,"E196"),sQuery(id+"F4.wireOp",EDGE,"E197"),sQuery(id+"F4.wireOp",EDGE,"E198"),sQuery(id+"F4.wireOp",EDGE,"E199"),sQuery(id+"F4.wireOp",EDGE,"E200"),sQuery(id+"F4.wireOp",EDGE,"E201"),sQuery(id+"F4.wireOp",EDGE,"E202"),sQuery(id+"F4.wireOp",EDGE,"E203"),sQuery(id+"F4.wireOp",EDGE,"E204"),sQuery(id+"F4.wireOp",EDGE,"E205"),sQuery(id+"F4.wireOp",EDGE,"E206"),sQuery(id+"F4.wireOp",EDGE,"E207"),sQuery(id+"F4.wireOp",EDGE,"E208"),sQuery(id+"F4.wireOp",EDGE,"E209"),sQuery(id+"F4.wireOp",EDGE,"E210"),sQuery(id+"F4.wireOp",EDGE,"E211"),sQuery(id+"F4.wireOp",EDGE,"E212"),sQuery(id+"F4.wireOp",EDGE,"E213"),sQuery(id+"F4.wireOp",EDGE,"E214"),sQuery(id+"F4.wireOp",EDGE,"E215"),sQuery(id+"F4.wireOp",EDGE,"E216"),sQuery(id+"F4.wireOp",EDGE,"E217"),sQuery(id+"F4.wireOp",EDGE,"E218"),sQuery(id+"F4.wireOp",EDGE,"E219"),sQuery(id+"F4.wireOp",EDGE,"E220"),sQuery(id+"F4.wireOp",EDGE,"E221"),sQuery(id+"F4.wireOp",EDGE,"E222"),sQuery(id+"F4.wireOp",EDGE,"E223"),sQuery(id+"F4.wireOp",EDGE,"E224"),sQuery(id+"F4.wireOp",EDGE,"E225"),sQuery(id+"F4.wireOp",EDGE,"E226"),sQuery(id+"F4.wireOp",EDGE,"E227"),sQuery(id+"F4.wireOp",EDGE,"E228"),sQuery(id+"F4.wireOp",EDGE,"E229"),sQuery(id+"F4.wireOp",EDGE,"E230"),sQuery(id+"F4.wireOp",EDGE,"E231"),sQuery(id+"F4.wireOp",EDGE,"E232"),sQuery(id+"F4.wireOp",EDGE,"E233"),sQuery(id+"F4.wireOp",EDGE,"E234"),sQuery(id+"F4.wireOp",EDGE,"E235"),sQuery(id+"F4.wireOp",EDGE,"E236"),sQuery(id+"F4.wireOp",EDGE,"E237"),sQuery(id+"F4.wireOp",EDGE,"E238"),sQuery(id+"F4.wireOp",EDGE,"E239"),sQuery(id+"F4.wireOp",EDGE,"E240"),sQuery(id+"F4.wireOp",EDGE,"E241"),sQuery(id+"F4.wireOp",EDGE,"E242"),sQuery(id+"F4.wireOp",EDGE,"E243"),sQuery(id+"F4.wireOp",EDGE,"E244"),sQuery(id+"F4.wireOp",EDGE,"E245"),sQuery(id+"F4.wireOp",EDGE,"E246"),sQuery(id+"F4.wireOp",EDGE,"E247"),sQuery(id+"F4.wireOp",EDGE,"E248"),sQuery(id+"F4.wireOp",EDGE,"E249"),sQuery(id+"F4.wireOp",EDGE,"E250"),sQuery(id+"F4.wireOp",EDGE,"E251"),sQuery(id+"F4.wireOp",EDGE,"E252"),sQuery(id+"F4.wireOp",EDGE,"E253"),sQuery(id+"F4.wireOp",EDGE,"E254"),sQuery(id+"F4.wireOp",EDGE,"E255"),sQuery(id+"F4.wireOp",EDGE,"E256"),sQuery(id+"F4.wireOp",EDGE,"E257"),sQuery(id+"F4.wireOp",EDGE,"E258"),sQuery(id+"F4.wireOp",EDGE,"E259"),sQuery(id+"F4.wireOp",EDGE,"E260"),sQuery(id+"F4.wireOp",EDGE,"E261"),sQuery(id+"F4.wireOp",EDGE,"E262"),sQuery(id+"F4.wireOp",EDGE,"E263"),sQuery(id+"F4.wireOp",EDGE,"E264"),sQuery(id+"F4.wireOp",EDGE,"E265"),sQuery(id+"F4.wireOp",EDGE,"E266"),sQuery(id+"F4.wireOp",EDGE,"E267"),sQuery(id+"F4.wireOp",EDGE,"E268"),sQuery(id+"F4.wireOp",EDGE,"E269"),sQuery(id+"F4.wireOp",EDGE,"E270"),sQuery(id+"F4.wireOp",EDGE,"E271"),sQuery(id+"F4.wireOp",EDGE,"E272"),sQuery(id+"F4.wireOp",EDGE,"E273"),sQuery(id+"F4.wireOp",EDGE,"E274"),sQuery(id+"F4.wireOp",EDGE,"E275"),sQuery(id+"F4.wireOp",EDGE,"E276"),sQuery(id+"F4.wireOp",EDGE,"E277"),sQuery(id+"F4.wireOp",EDGE,"E278"),sQuery(id+"F4.wireOp",EDGE,"E279"),sQuery(id+"F4.wireOp",EDGE,"E280"),sQuery(id+"F4.wireOp",EDGE,"E281"),sQuery(id+"F4.wireOp",EDGE,"E282"),sQuery(id+"F4.wireOp",EDGE,"E283"),sQuery(id+"F4.wireOp",EDGE,"E284"),sQuery(id+"F4.wireOp",EDGE,"E285"),sQuery(id+"F4.wireOp",EDGE,"E286"),sQuery(id+"F4.wireOp",EDGE,"E287"),sQuery(id+"F4.wireOp",EDGE,"E288"),sQuery(id+"F4.wireOp",EDGE,"E289"),sQuery(id+"F4.wireOp",EDGE,"E290"),sQuery(id+"F4.wireOp",EDGE,"E291"),sQuery(id+"F4.wireOp",EDGE,"E292"),sQuery(id+"F4.wireOp",EDGE,"E293"),sQuery(id+"F4.wireOp",EDGE,"E294"),sQuery(id+"F4.wireOp",EDGE,"E295"),sQuery(id+"F4.wireOp",EDGE,"E296"),sQuery(id+"F4.wireOp",EDGE,"E297"),sQuery(id+"F4.wireOp",EDGE,"E298"),sQuery(id+"F4.wireOp",EDGE,"E299"),sQuery(id+"F4.wireOp",EDGE,"E300"),sQuery(id+"F4.wireOp",EDGE,"E301"),sQuery(id+"F4.wireOp",EDGE,"E302"),sQuery(id+"F4.wireOp",EDGE,"E303"),sQuery(id+"F4.wireOp",EDGE,"E304"),sQuery(id+"F4.wireOp",EDGE,"E305"),sQuery(id+"F4.wireOp",EDGE,"E306"),sQuery(id+"F4.wireOp",EDGE,"E307"),sQuery(id+"F4.wireOp",EDGE,"E308"),sQuery(id+"F4.wireOp",EDGE,"E309"),sQuery(id+"F4.wireOp",EDGE,"E310"),sQuery(id+"F4.wireOp",EDGE,"E311"),sQuery(id+"F4.wireOp",EDGE,"E312"),sQuery(id+"F4.wireOp",EDGE,"E313"),sQuery(id+"F4.wireOp",EDGE,"E314"),sQuery(id+"F4.wireOp",EDGE,"E315"),sQuery(id+"F4.wireOp",EDGE,"E316"),sQuery(id+"F4.wireOp",EDGE,"E317"),sQuery(id+"F4.wireOp",EDGE,"E318"),sQuery(id+"F4.wireOp",EDGE,"E319"),sQuery(id+"F4.wireOp",EDGE,"E320"),sQuery(id+"F4.wireOp",EDGE,"E321"),sQuery(id+"F4.wireOp",EDGE,"E322"),sQuery(id+"F4.wireOp",EDGE,"E323"),sQuery(id+"F4.wireOp",EDGE,"E324"),sQuery(id+"F4.wireOp",EDGE,"E325"),sQuery(id+"F4.wireOp",EDGE,"E326"),sQuery(id+"F4.wireOp",EDGE,"E327"),sQuery(id+"F4.wireOp",EDGE,"E328"),sQuery(id+"F4.wireOp",EDGE,"E329"),sQuery(id+"F4.wireOp",EDGE,"E330"),sQuery(id+"F4.wireOp",EDGE,"E331"),sQuery(id+"F4.wireOp",EDGE,"E332"),sQuery(id+"F4.wireOp",EDGE,"E333"),sQuery(id+"F4.wireOp",EDGE,"E334"),sQuery(id+"F4.wireOp",EDGE,"E335"),sQuery(id+"F4.wireOp",EDGE,"E336"),sQuery(id+"F4.wireOp",EDGE,"E337"),sQuery(id+"F4.wireOp",EDGE,"E338"),sQuery(id+"F4.wireOp",EDGE,"E339"),sQuery(id+"F4.wireOp",EDGE,"E340"),sQuery(id+"F4.wireOp",EDGE,"E341"),sQuery(id+"F4.wireOp",EDGE,"E342"),sQuery(id+"F4.wireOp",EDGE,"E343"),sQuery(id+"F4.wireOp",EDGE,"E344"),sQuery(id+"F4.wireOp",EDGE,"E345"),sQuery(id+"F4.wireOp",EDGE,"E346"),sQuery(id+"F4.wireOp",EDGE,"E347"),sQuery(id+"F4.wireOp",EDGE,"E348")])],"isStart":false});
            var sketch = newSketch(context, id + "F9", { "sketchPlane" : qUnion([Q0])});
            skCircle(sketch, "E351.0", {"center": v(0, 0) * mm, "radius": 9.05 * mm});
            skSolve(sketch);
        }
        {
            var Q0;
            Q0=makeQuery(id+"F9.imprint","IMPRINT",FACE,{"disambiguationData":[TD([[makeQuery(id+"F9.imprint","IMPRINT",EDGE,{"derivedFrom":sQuery(id+"F9.wireOp",EDGE,"E351.0")}),1.0]])]});
            extrude(context, id + "F10", {"entities" : qUnion([Q0]), "operationType" : NewBodyOperationType.REMOVE, "endBound" : BoundingType.THROUGH_ALL, "oppositeDirection" : true, "depth" : 25 * mm});
        }
    });
